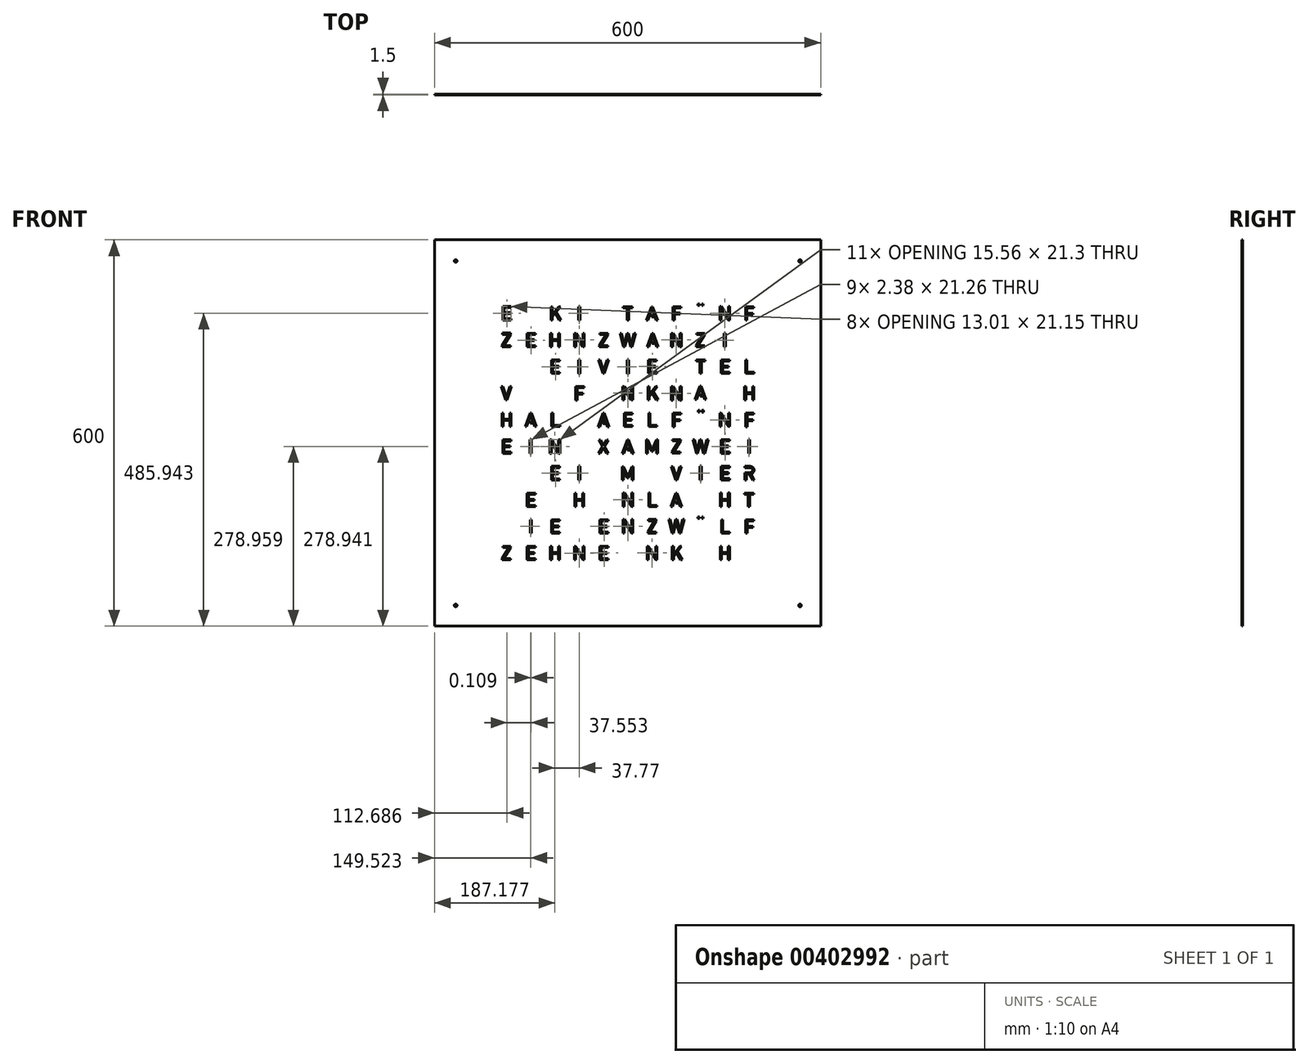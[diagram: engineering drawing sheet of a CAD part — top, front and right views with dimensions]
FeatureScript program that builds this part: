
annotation { "Feature Type Name" : "Feature", "Feature Type Description" : "" }
export const myFeature = defineFeature(function(context is Context, id is Id, definition is map)
    precondition{}
    {
        {
            var Q0;
            Q0=qCreatedBy(makeId("Front.planeOp"),FACE);
            var sketch = newSketch(context, id + "F0", { "sketchPlane" : qUnion([Q0])});
            skLineSegment(sketch, "E0", {"start": v(188.56, 142.8) * mm, "end": v(188.56, 145) * mm});
            skLineSegment(sketch, "E1", {"start": v(188.56, 145) * mm, "end": v(196.13, 145) * mm});
            skLineSegment(sketch, "E2", {"start": v(196.13, 145) * mm, "end": v(196.13, 140.53) * mm});
            skLineSegment(sketch, "E3", {"start": v(188.56, 142.8) * mm, "end": v(194.09, 142.8) * mm});
            skLineSegment(sketch, "E4", {"start": v(194.09, 142.8) * mm, "end": v(194.09, 140.53) * mm});
            skArc(sketch, "E5", {"start": v(183.68, 140.53) * mm, "mid": v(188.88, 135.76) * mm, "end": v(194.09, 140.53) * mm});
            skArc(sketch, "E6", {"start": v(181.41, 140.53) * mm, "mid": v(188.77, 133.64) * mm, "end": v(196.13, 140.53) * mm});
            skLineSegment(sketch, "E7", {"start": v(181.41, 140.53) * mm, "end": v(181.41, 148.36) * mm});
            skLineSegment(sketch, "E8", {"start": v(196.13, 148.36) * mm, "end": v(194.09, 148.36) * mm});
            skLineSegment(sketch, "E9", {"start": v(183.68, 140.53) * mm, "end": v(183.68, 148.36) * mm});
            skArc(sketch, "E10", {"start": v(196.13, 148.36) * mm, "mid": v(188.77, 155.1) * mm, "end": v(181.41, 148.36) * mm});
            skArc(sketch, "E11", {"start": v(194.08, 148.36) * mm, "mid": v(188.88, 153.17) * mm, "end": v(183.68, 148.36) * mm});
            skLineSegment(sketch, "E12", {"start": v(-300, -300) * mm, "end": v(-300, 300) * mm});
            skLineSegment(sketch, "E13", {"start": v(-300, 300) * mm, "end": v(300, 300) * mm});
            skLineSegment(sketch, "E14", {"start": v(300, 300) * mm, "end": v(300, -300) * mm});
            skLineSegment(sketch, "E15", {"start": v(300, -300) * mm, "end": v(-300, -300) * mm});
            skLineSegment(sketch, "E16", {"start": v(149.86, 133.65) * mm, "end": v(149.86, 154.9) * mm});
            skLineSegment(sketch, "E17", {"start": v(149.86, 154.9) * mm, "end": v(152.25, 154.9) * mm});
            skLineSegment(sketch, "E18", {"start": v(152.25, 154.9) * mm, "end": v(152.25, 133.65) * mm});
            skLineSegment(sketch, "E19", {"start": v(152.25, 133.65) * mm, "end": v(149.86, 133.65) * mm});
            skLineSegment(sketch, "E20", {"start": v(107.48, 155) * mm, "end": v(120.12, 155) * mm});
            skLineSegment(sketch, "E21", {"start": v(120.12, 155) * mm, "end": v(120.12, 152.77) * mm});
            skLineSegment(sketch, "E22", {"start": v(120.12, 152.77) * mm, "end": v(109.33, 135.7) * mm});
            skLineSegment(sketch, "E23", {"start": v(109.33, 135.7) * mm, "end": v(119.96, 135.7) * mm});
            skLineSegment(sketch, "E24", {"start": v(119.96, 135.7) * mm, "end": v(119.96, 133.7) * mm});
            skLineSegment(sketch, "E25", {"start": v(119.96, 133.7) * mm, "end": v(106.84, 133.7) * mm});
            skLineSegment(sketch, "E26", {"start": v(106.84, 133.7) * mm, "end": v(106.84, 135.7) * mm});
            skLineSegment(sketch, "E27", {"start": v(106.84, 135.7) * mm, "end": v(117.5, 152.77) * mm});
            skLineSegment(sketch, "E28", {"start": v(117.5, 152.77) * mm, "end": v(107.48, 152.77) * mm});
            skLineSegment(sketch, "E29", {"start": v(107.48, 152.77) * mm, "end": v(107.48, 155) * mm});
            skLineSegment(sketch, "E30", {"start": v(83.43, 133.7) * mm, "end": v(83.43, 155) * mm});
            skLineSegment(sketch, "E31", {"start": v(83.43, 155) * mm, "end": v(81.25, 155) * mm});
            skLineSegment(sketch, "E32", {"start": v(81.25, 155) * mm, "end": v(81.25, 137.64) * mm});
            skLineSegment(sketch, "E33", {"start": v(81.25, 137.64) * mm, "end": v(70.14, 155) * mm});
            skLineSegment(sketch, "E34", {"start": v(70.14, 155) * mm, "end": v(67.87, 155) * mm});
            skLineSegment(sketch, "E35", {"start": v(67.87, 155) * mm, "end": v(67.87, 133.7) * mm});
            skLineSegment(sketch, "E36", {"start": v(67.87, 133.7) * mm, "end": v(70.14, 133.7) * mm});
            skLineSegment(sketch, "E37", {"start": v(70.14, 133.7) * mm, "end": v(70.14, 150.6) * mm});
            skLineSegment(sketch, "E38", {"start": v(70.14, 150.6) * mm, "end": v(81.25, 133.7) * mm});
            skLineSegment(sketch, "E39", {"start": v(81.25, 133.7) * mm, "end": v(83.43, 133.7) * mm});
            skLineSegment(sketch, "E40", {"start": v(38.16, 138.74) * mm, "end": v(38.16, 140.9) * mm});
            skLineSegment(sketch, "E41", {"start": v(38.16, 140.9) * mm, "end": v(42.67, 140.9) * mm});
            skLineSegment(sketch, "E42", {"start": v(38.16, 138.74) * mm, "end": v(43.46, 138.75) * mm});
            skLineSegment(sketch, "E43", {"start": v(47.66, 133.7) * mm, "end": v(45.24, 133.7) * mm});
            skLineSegment(sketch, "E44", {"start": v(45.24, 133.7) * mm, "end": v(43.46, 138.75) * mm});
            skLineSegment(sketch, "E45", {"start": v(39.07, 151.34) * mm, "end": v(32.75, 133.7) * mm});
            skLineSegment(sketch, "E46", {"start": v(32.75, 133.7) * mm, "end": v(30.26, 133.7) * mm});
            skLineSegment(sketch, "E47", {"start": v(30.26, 133.7) * mm, "end": v(38.13, 154.86) * mm});
            skLineSegment(sketch, "E48", {"start": v(38.13, 154.86) * mm, "end": v(39.83, 154.86) * mm});
            skLineSegment(sketch, "E49", {"start": v(39.83, 154.86) * mm, "end": v(47.66, 133.7) * mm});
            skLineSegment(sketch, "E50", {"start": v(42.67, 140.9) * mm, "end": v(39.07, 151.34) * mm});
            skLineSegment(sketch, "E51", {"start": v(6.99, 133.7) * mm, "end": v(4.75, 133.7) * mm});
            skLineSegment(sketch, "E52", {"start": v(4.75, 133.7) * mm, "end": v(0.21, 150.41) * mm});
            skLineSegment(sketch, "E53", {"start": v(0.21, 150.41) * mm, "end": v(-4.4, 133.7) * mm});
            skLineSegment(sketch, "E54", {"start": v(-4.4, 133.7) * mm, "end": v(-6.22, 133.7) * mm});
            skLineSegment(sketch, "E55", {"start": v(-6.22, 133.7) * mm, "end": v(-11.55, 154.84) * mm});
            skLineSegment(sketch, "E56", {"start": v(-11.55, 154.84) * mm, "end": v(-9.36, 154.84) * mm});
            skLineSegment(sketch, "E57", {"start": v(-9.36, 154.84) * mm, "end": v(-5.35, 137.97) * mm});
            skLineSegment(sketch, "E58", {"start": v(-5.35, 137.97) * mm, "end": v(-0.84, 154.84) * mm});
            skLineSegment(sketch, "E59", {"start": v(-0.84, 154.84) * mm, "end": v(1.31, 154.84) * mm});
            skLineSegment(sketch, "E60", {"start": v(1.31, 154.84) * mm, "end": v(5.78, 137.97) * mm});
            skLineSegment(sketch, "E61", {"start": v(5.78, 137.97) * mm, "end": v(10.05, 154.84) * mm});
            skLineSegment(sketch, "E62", {"start": v(10.05, 154.84) * mm, "end": v(12.36, 154.84) * mm});
            skLineSegment(sketch, "E63", {"start": v(12.36, 154.84) * mm, "end": v(6.99, 133.7) * mm});
            skLineSegment(sketch, "E64", {"start": v(-119.95, 133.65) * mm, "end": v(-119.95, 154.8) * mm});
            skLineSegment(sketch, "E65", {"start": v(-119.95, 154.8) * mm, "end": v(-117.8, 154.8) * mm});
            skLineSegment(sketch, "E66", {"start": v(-117.8, 154.8) * mm, "end": v(-117.8, 145.23) * mm});
            skLineSegment(sketch, "E67", {"start": v(-117.8, 145.23) * mm, "end": v(-107.7, 145.23) * mm});
            skLineSegment(sketch, "E68", {"start": v(-107.7, 145.23) * mm, "end": v(-107.7, 154.8) * mm});
            skLineSegment(sketch, "E69", {"start": v(-107.7, 154.8) * mm, "end": v(-105.57, 154.8) * mm});
            skLineSegment(sketch, "E70", {"start": v(-105.57, 154.8) * mm, "end": v(-105.57, 133.65) * mm});
            skLineSegment(sketch, "E71", {"start": v(-105.57, 133.65) * mm, "end": v(-107.7, 133.65) * mm});
            skLineSegment(sketch, "E72", {"start": v(-107.7, 133.65) * mm, "end": v(-107.7, 143.34) * mm});
            skLineSegment(sketch, "E73", {"start": v(-107.7, 143.34) * mm, "end": v(-117.8, 143.34) * mm});
            skLineSegment(sketch, "E74", {"start": v(-117.8, 143.34) * mm, "end": v(-117.8, 133.65) * mm});
            skLineSegment(sketch, "E75", {"start": v(-117.8, 133.65) * mm, "end": v(-119.95, 133.65) * mm});
            skLineSegment(sketch, "E76", {"start": v(-143.25, 133.65) * mm, "end": v(-156.27, 133.65) * mm});
            skLineSegment(sketch, "E77", {"start": v(-156.27, 133.65) * mm, "end": v(-156.27, 154.8) * mm});
            skLineSegment(sketch, "E78", {"start": v(-156.27, 154.8) * mm, "end": v(-143.33, 154.8) * mm});
            skLineSegment(sketch, "E79", {"start": v(-143.33, 154.8) * mm, "end": v(-143.33, 152.78) * mm});
            skLineSegment(sketch, "E80", {"start": v(-143.33, 152.78) * mm, "end": v(-154.07, 152.78) * mm});
            skLineSegment(sketch, "E81", {"start": v(-154.07, 152.78) * mm, "end": v(-154.07, 145.25) * mm});
            skLineSegment(sketch, "E82", {"start": v(-154.07, 145.25) * mm, "end": v(-144.92, 145.25) * mm});
            skLineSegment(sketch, "E83", {"start": v(-144.92, 145.25) * mm, "end": v(-144.92, 143.28) * mm});
            skLineSegment(sketch, "E84", {"start": v(-144.92, 143.28) * mm, "end": v(-154.07, 143.28) * mm});
            skLineSegment(sketch, "E85", {"start": v(-154.07, 143.28) * mm, "end": v(-154.07, 135.67) * mm});
            skLineSegment(sketch, "E86", {"start": v(-154.07, 135.67) * mm, "end": v(-143.25, 135.67) * mm});
            skLineSegment(sketch, "E87", {"start": v(-143.25, 135.67) * mm, "end": v(-143.25, 133.65) * mm});
            skLineSegment(sketch, "E88", {"start": v(-119.17, 175.05) * mm, "end": v(-119.17, 196.27) * mm});
            skLineSegment(sketch, "E89", {"start": v(-119.17, 196.27) * mm, "end": v(-116.98, 196.27) * mm});
            skLineSegment(sketch, "E90", {"start": v(-116.98, 196.27) * mm, "end": v(-116.98, 183.75) * mm});
            skLineSegment(sketch, "E91", {"start": v(-116.98, 183.75) * mm, "end": v(-106.88, 196.27) * mm});
            skLineSegment(sketch, "E92", {"start": v(-106.88, 196.27) * mm, "end": v(-104.38, 196.27) * mm});
            skLineSegment(sketch, "E93", {"start": v(-104.38, 196.27) * mm, "end": v(-111.04, 188.07) * mm});
            skLineSegment(sketch, "E94", {"start": v(-111.04, 188.07) * mm, "end": v(-103.4, 175.05) * mm});
            skLineSegment(sketch, "E95", {"start": v(-103.4, 175.05) * mm, "end": v(-105.9, 175.05) * mm});
            skLineSegment(sketch, "E96", {"start": v(-105.9, 175.05) * mm, "end": v(-112.44, 186.29) * mm});
            skLineSegment(sketch, "E97", {"start": v(-112.44, 186.29) * mm, "end": v(-116.98, 180.61) * mm});
            skLineSegment(sketch, "E98", {"start": v(-116.98, 180.61) * mm, "end": v(-116.98, 175.05) * mm});
            skLineSegment(sketch, "E99", {"start": v(-116.98, 175.05) * mm, "end": v(-119.17, 175.05) * mm});
            skLineSegment(sketch, "E100", {"start": v(-0.86, 175.05) * mm, "end": v(1.57, 175.05) * mm});
            skLineSegment(sketch, "E101", {"start": v(1.57, 175.05) * mm, "end": v(1.57, 194.25) * mm});
            skLineSegment(sketch, "E102", {"start": v(1.57, 194.25) * mm, "end": v(7.58, 194.25) * mm});
            skLineSegment(sketch, "E103", {"start": v(7.58, 194.25) * mm, "end": v(7.58, 196.28) * mm});
            skLineSegment(sketch, "E104", {"start": v(7.58, 196.28) * mm, "end": v(-6.84, 196.28) * mm});
            skLineSegment(sketch, "E105", {"start": v(-6.84, 196.28) * mm, "end": v(-6.84, 194.25) * mm});
            skLineSegment(sketch, "E106", {"start": v(-6.84, 194.25) * mm, "end": v(-0.86, 194.25) * mm});
            skLineSegment(sketch, "E107", {"start": v(-0.86, 194.25) * mm, "end": v(-0.86, 175.05) * mm});
            skLineSegment(sketch, "E108", {"start": v(-67.18, 133.7) * mm, "end": v(-67.18, 155) * mm});
            skLineSegment(sketch, "E109", {"start": v(-67.18, 155) * mm, "end": v(-69.36, 155) * mm});
            skLineSegment(sketch, "E110", {"start": v(-69.36, 155) * mm, "end": v(-69.36, 137.64) * mm});
            skLineSegment(sketch, "E111", {"start": v(-69.36, 137.64) * mm, "end": v(-80.47, 155) * mm});
            skLineSegment(sketch, "E112", {"start": v(-80.47, 155) * mm, "end": v(-82.74, 155) * mm});
            skLineSegment(sketch, "E113", {"start": v(-82.74, 155) * mm, "end": v(-82.74, 133.7) * mm});
            skLineSegment(sketch, "E114", {"start": v(-82.74, 133.7) * mm, "end": v(-80.47, 133.7) * mm});
            skLineSegment(sketch, "E115", {"start": v(-80.47, 133.7) * mm, "end": v(-80.47, 150.6) * mm});
            skLineSegment(sketch, "E116", {"start": v(-80.47, 150.6) * mm, "end": v(-69.36, 133.7) * mm});
            skLineSegment(sketch, "E117", {"start": v(-69.36, 133.7) * mm, "end": v(-67.18, 133.7) * mm});
            skLineSegment(sketch, "E118", {"start": v(-43.37, 155) * mm, "end": v(-30.74, 155) * mm});
            skLineSegment(sketch, "E119", {"start": v(-30.74, 155) * mm, "end": v(-30.74, 152.77) * mm});
            skLineSegment(sketch, "E120", {"start": v(-30.74, 152.77) * mm, "end": v(-41.52, 135.7) * mm});
            skLineSegment(sketch, "E121", {"start": v(-41.52, 135.7) * mm, "end": v(-30.89, 135.7) * mm});
            skLineSegment(sketch, "E122", {"start": v(-30.89, 135.7) * mm, "end": v(-30.89, 133.7) * mm});
            skLineSegment(sketch, "E123", {"start": v(-30.89, 133.7) * mm, "end": v(-44.01, 133.7) * mm});
            skLineSegment(sketch, "E124", {"start": v(-44.01, 133.7) * mm, "end": v(-44.01, 135.7) * mm});
            skLineSegment(sketch, "E125", {"start": v(-44.01, 135.7) * mm, "end": v(-33.35, 152.77) * mm});
            skLineSegment(sketch, "E126", {"start": v(-33.35, 152.77) * mm, "end": v(-43.37, 152.77) * mm});
            skLineSegment(sketch, "E127", {"start": v(-43.37, 152.77) * mm, "end": v(-43.37, 155) * mm});
            skLineSegment(sketch, "E128", {"start": v(-70.28, -14.49) * mm, "end": v(-68.78, -12.92) * mm});
            skLineSegment(sketch, "E129", {"start": v(-82.63, -29.02) * mm, "end": v(-80.97, -27.45) * mm});
            skArc(sketch, "E130", {"start": v(-70.29, -14.49) * mm, "mid": v(-72.17, -13.04) * mm, "end": v(-74.5, -12.5) * mm});
            skArc(sketch, "E131", {"start": v(-68.78, -12.92) * mm, "mid": v(-71.36, -11) * mm, "end": v(-74.5, -10.31) * mm});
            skLineSegment(sketch, "E132", {"start": v(-74.5, -12.5) * mm, "end": v(-76.2, -12.5) * mm});
            skArc(sketch, "E133", {"start": v(-76.2, -12.5) * mm, "mid": v(-79.8, -15.86) * mm, "end": v(-76.68, -19.67) * mm});
            skLineSegment(sketch, "E134", {"start": v(-76.68, -19.67) * mm, "end": v(-72.97, -20.28) * mm});
            skLineSegment(sketch, "E135", {"start": v(-74.5, -10.31) * mm, "end": v(-76.49, -10.31) * mm});
            skArc(sketch, "E136", {"start": v(-76.49, -10.31) * mm, "mid": v(-81.97, -15.85) * mm, "end": v(-76.98, -21.83) * mm});
            skLineSegment(sketch, "E137", {"start": v(-76.98, -21.83) * mm, "end": v(-73.61, -22.28) * mm});
            skArc(sketch, "E138", {"start": v(-80.97, -27.45) * mm, "mid": v(-79.05, -28.97) * mm, "end": v(-76.72, -29.74) * mm});
            skLineSegment(sketch, "E139", {"start": v(-76.72, -29.74) * mm, "end": v(-73.89, -29.74) * mm});
            skArc(sketch, "E140", {"start": v(-73.9, -29.73) * mm, "mid": v(-70.2, -26.14) * mm, "end": v(-73.61, -22.28) * mm});
            skArc(sketch, "E141", {"start": v(-82.63, -29.02) * mm, "mid": v(-79.89, -31.2) * mm, "end": v(-76.48, -31.97) * mm});
            skLineSegment(sketch, "E142", {"start": v(-76.48, -31.97) * mm, "end": v(-73.95, -31.97) * mm});
            skArc(sketch, "E143", {"start": v(-73.95, -31.97) * mm, "mid": v(-68.13, -26.57) * mm, "end": v(-72.97, -20.28) * mm});
            skLineSegment(sketch, "E144", {"start": v(70.3, 196.29) * mm, "end": v(70.3, 174.95) * mm});
            skLineSegment(sketch, "E145", {"start": v(70.3, 174.95) * mm, "end": v(72.58, 174.95) * mm});
            skLineSegment(sketch, "E146", {"start": v(72.58, 174.95) * mm, "end": v(72.58, 184.33) * mm});
            skLineSegment(sketch, "E147", {"start": v(72.58, 184.33) * mm, "end": v(81.7, 184.33) * mm});
            skLineSegment(sketch, "E148", {"start": v(81.7, 184.33) * mm, "end": v(81.7, 186.22) * mm});
            skLineSegment(sketch, "E149", {"start": v(81.7, 186.22) * mm, "end": v(72.58, 186.22) * mm});
            skLineSegment(sketch, "E150", {"start": v(72.58, 186.22) * mm, "end": v(72.58, 194.17) * mm});
            skLineSegment(sketch, "E151", {"start": v(72.58, 194.17) * mm, "end": v(83.24, 194.17) * mm});
            skLineSegment(sketch, "E152", {"start": v(83.24, 194.17) * mm, "end": v(83.24, 196.29) * mm});
            skLineSegment(sketch, "E153", {"start": v(83.24, 196.29) * mm, "end": v(70.3, 196.29) * mm});
            skLineSegment(sketch, "E154", {"start": v(112.3, 92.35) * mm, "end": v(114.73, 92.35) * mm});
            skLineSegment(sketch, "E155", {"start": v(114.73, 92.35) * mm, "end": v(114.73, 111.55) * mm});
            skLineSegment(sketch, "E156", {"start": v(114.73, 111.55) * mm, "end": v(120.74, 111.55) * mm});
            skLineSegment(sketch, "E157", {"start": v(120.74, 111.55) * mm, "end": v(120.74, 113.58) * mm});
            skLineSegment(sketch, "E158", {"start": v(120.74, 113.58) * mm, "end": v(106.32, 113.58) * mm});
            skLineSegment(sketch, "E159", {"start": v(106.32, 113.58) * mm, "end": v(106.32, 111.55) * mm});
            skLineSegment(sketch, "E160", {"start": v(106.32, 111.55) * mm, "end": v(112.3, 111.55) * mm});
            skLineSegment(sketch, "E161", {"start": v(112.3, 111.55) * mm, "end": v(112.3, 92.35) * mm});
            skLineSegment(sketch, "E162", {"start": v(109.41, 200.52) * mm, "end": v(109.41, 197.83) * mm});
            skLineSegment(sketch, "E163", {"start": v(109.41, 197.83) * mm, "end": v(111.54, 197.83) * mm});
            skLineSegment(sketch, "E164", {"start": v(111.54, 197.83) * mm, "end": v(111.54, 200.52) * mm});
            skLineSegment(sketch, "E165", {"start": v(111.54, 200.52) * mm, "end": v(109.41, 200.52) * mm});
            skLineSegment(sketch, "E166", {"start": v(115.37, 200.52) * mm, "end": v(115.37, 197.83) * mm});
            skLineSegment(sketch, "E167", {"start": v(115.37, 197.83) * mm, "end": v(117.5, 197.83) * mm});
            skLineSegment(sketch, "E168", {"start": v(117.5, 197.83) * mm, "end": v(117.5, 200.52) * mm});
            skLineSegment(sketch, "E169", {"start": v(117.5, 200.52) * mm, "end": v(115.37, 200.52) * mm});
            skLineSegment(sketch, "E170", {"start": v(106.2, 181.56) * mm, "end": v(106.2, 196.32) * mm});
            skLineSegment(sketch, "E171", {"start": v(106.2, 196.32) * mm, "end": v(108.28, 196.32) * mm});
            skLineSegment(sketch, "E172", {"start": v(108.28, 196.32) * mm, "end": v(108.28, 181.56) * mm});
            skArc(sketch, "E173", {"start": v(106.2, 181.56) * mm, "mid": v(113.48, 174.84) * mm, "end": v(120.76, 181.56) * mm});
            skArc(sketch, "E174", {"start": v(108.27, 181.56) * mm, "mid": v(113.38, 176.92) * mm, "end": v(118.49, 181.56) * mm});
            skLineSegment(sketch, "E175", {"start": v(118.49, 181.56) * mm, "end": v(118.49, 196.32) * mm});
            skLineSegment(sketch, "E176", {"start": v(118.49, 196.32) * mm, "end": v(120.76, 196.32) * mm});
            skLineSegment(sketch, "E177", {"start": v(120.76, 196.32) * mm, "end": v(120.76, 181.56) * mm});
            skLineSegment(sketch, "E178", {"start": v(183.41, 92.29) * mm, "end": v(183.41, 113.36) * mm});
            skLineSegment(sketch, "E179", {"start": v(183.41, 113.36) * mm, "end": v(185.53, 113.36) * mm});
            skLineSegment(sketch, "E180", {"start": v(185.53, 113.36) * mm, "end": v(185.53, 94.21) * mm});
            skLineSegment(sketch, "E181", {"start": v(185.53, 94.21) * mm, "end": v(196.43, 94.21) * mm});
            skLineSegment(sketch, "E182", {"start": v(196.43, 94.21) * mm, "end": v(196.43, 92.29) * mm});
            skLineSegment(sketch, "E183", {"start": v(196.43, 92.29) * mm, "end": v(183.41, 92.29) * mm});
            skLineSegment(sketch, "E184", {"start": v(156.21, 65.56) * mm, "end": v(158.39, 65.56) * mm});
            skLineSegment(sketch, "E185", {"start": v(156.36, 57.27) * mm, "end": v(158.3, 57.27) * mm});
            skLineSegment(sketch, "E186", {"start": v(146, 65.78) * mm, "end": v(146, 58.67) * mm});
            skLineSegment(sketch, "E187", {"start": v(143.88, 65.56) * mm, "end": v(143.88, 57.16) * mm});
            skArc(sketch, "E188", {"start": v(156.21, 65.56) * mm, "mid": v(151.2, 70.29) * mm, "end": v(146, 65.78) * mm});
            skArc(sketch, "E189", {"start": v(158.39, 65.56) * mm, "mid": v(151.13, 72.37) * mm, "end": v(143.88, 65.55) * mm});
            skArc(sketch, "E190", {"start": v(146, 58.67) * mm, "mid": v(150.5, 52.93) * mm, "end": v(156.36, 57.27) * mm});
            skArc(sketch, "E191", {"start": v(143.88, 57.16) * mm, "mid": v(151.14, 50.64) * mm, "end": v(158.3, 57.27) * mm});
            skLineSegment(sketch, "E192", {"start": v(-38.4, 92.3) * mm, "end": v(-45.18, 113.29) * mm});
            skLineSegment(sketch, "E193", {"start": v(-45.18, 113.29) * mm, "end": v(-42.72, 113.29) * mm});
            skLineSegment(sketch, "E194", {"start": v(-42.72, 113.29) * mm, "end": v(-37.31, 96.53) * mm});
            skLineSegment(sketch, "E195", {"start": v(-37.31, 96.53) * mm, "end": v(-31.86, 113.29) * mm});
            skLineSegment(sketch, "E196", {"start": v(-31.86, 113.29) * mm, "end": v(-29.52, 113.29) * mm});
            skLineSegment(sketch, "E197", {"start": v(-29.52, 113.29) * mm, "end": v(-36.48, 92.3) * mm});
            skLineSegment(sketch, "E198", {"start": v(-36.48, 92.3) * mm, "end": v(-38.4, 92.3) * mm});
            skLineSegment(sketch, "E199", {"start": v(29.1, -31.6) * mm, "end": v(29.1, -10.57) * mm});
            skLineSegment(sketch, "E200", {"start": v(29.1, -10.57) * mm, "end": v(31.14, -10.57) * mm});
            skLineSegment(sketch, "E201", {"start": v(31.14, -10.57) * mm, "end": v(38.06, -26.2) * mm});
            skLineSegment(sketch, "E202", {"start": v(38.06, -26.2) * mm, "end": v(44.87, -10.57) * mm});
            skLineSegment(sketch, "E203", {"start": v(44.87, -10.57) * mm, "end": v(46.77, -10.57) * mm});
            skLineSegment(sketch, "E204", {"start": v(46.77, -10.57) * mm, "end": v(46.77, -31.6) * mm});
            skLineSegment(sketch, "E205", {"start": v(46.77, -31.6) * mm, "end": v(44.87, -31.6) * mm});
            skLineSegment(sketch, "E206", {"start": v(44.87, -31.6) * mm, "end": v(44.87, -15.64) * mm});
            skLineSegment(sketch, "E207", {"start": v(44.87, -15.64) * mm, "end": v(38.97, -28.73) * mm});
            skLineSegment(sketch, "E208", {"start": v(38.97, -28.73) * mm, "end": v(37.2, -28.73) * mm});
            skLineSegment(sketch, "E209", {"start": v(37.2, -28.73) * mm, "end": v(31.07, -15.15) * mm});
            skLineSegment(sketch, "E210", {"start": v(31.07, -15.15) * mm, "end": v(31.07, -31.6) * mm});
            skLineSegment(sketch, "E211", {"start": v(31.07, -31.6) * mm, "end": v(29.1, -31.6) * mm});
            skLineSegment(sketch, "E212", {"start": v(-45.1, -31.67) * mm, "end": v(-42.56, -31.67) * mm});
            skLineSegment(sketch, "E213", {"start": v(-42.56, -31.67) * mm, "end": v(-37.5, -22.97) * mm});
            skLineSegment(sketch, "E214", {"start": v(-37.5, -22.97) * mm, "end": v(-32.38, -31.67) * mm});
            skLineSegment(sketch, "E215", {"start": v(-32.38, -31.67) * mm, "end": v(-29.85, -31.67) * mm});
            skLineSegment(sketch, "E216", {"start": v(-29.85, -31.67) * mm, "end": v(-36.4, -20.96) * mm});
            skLineSegment(sketch, "E217", {"start": v(-36.4, -20.96) * mm, "end": v(-30.2, -10.64) * mm});
            skLineSegment(sketch, "E218", {"start": v(-30.2, -10.64) * mm, "end": v(-32.65, -10.64) * mm});
            skLineSegment(sketch, "E219", {"start": v(-32.65, -10.64) * mm, "end": v(-37.5, -19.11) * mm});
            skLineSegment(sketch, "E220", {"start": v(-37.5, -19.11) * mm, "end": v(-42.22, -10.64) * mm});
            skLineSegment(sketch, "E221", {"start": v(-42.22, -10.64) * mm, "end": v(-44.64, -10.64) * mm});
            skLineSegment(sketch, "E222", {"start": v(-44.64, -10.64) * mm, "end": v(-38.63, -21.08) * mm});
            skLineSegment(sketch, "E223", {"start": v(-38.63, -21.08) * mm, "end": v(-45.1, -31.67) * mm});
            skLineSegment(sketch, "E224", {"start": v(-195.05, 99.84) * mm, "end": v(-195.05, 113.34) * mm});
            skLineSegment(sketch, "E225", {"start": v(-195.05, 113.34) * mm, "end": v(-187, 113.34) * mm});
            skLineSegment(sketch, "E226", {"start": v(-195.05, 99.84) * mm, "end": v(-192.82, 99.84) * mm});
            skLineSegment(sketch, "E227", {"start": v(-192.82, 99.84) * mm, "end": v(-192.82, 111.53) * mm});
            skLineSegment(sketch, "E228", {"start": v(-192.82, 111.53) * mm, "end": v(-187.13, 111.53) * mm});
            skArc(sketch, "E229", {"start": v(-180.57, 106.68) * mm, "mid": v(-182.44, 111.3) * mm, "end": v(-187, 113.34) * mm});
            skArc(sketch, "E230", {"start": v(-182.6, 107.52) * mm, "mid": v(-184.16, 110.32) * mm, "end": v(-187.13, 111.53) * mm});
            skLineSegment(sketch, "E231", {"start": v(-182.6, 107.52) * mm, "end": v(-182.6, 98.82) * mm});
            skLineSegment(sketch, "E232", {"start": v(-180.56, 106.69) * mm, "end": v(-180.56, 98.85) * mm});
            skLineSegment(sketch, "E233", {"start": v(-195.05, 94.35) * mm, "end": v(-195.05, 92.3) * mm});
            skLineSegment(sketch, "E234", {"start": v(-195.05, 92.3) * mm, "end": v(-187.8, 92.3) * mm});
            skLineSegment(sketch, "E235", {"start": v(-195.05, 94.35) * mm, "end": v(-187.24, 94.35) * mm});
            skArc(sketch, "E236", {"start": v(-187.24, 94.35) * mm, "mid": v(-184.08, 95.71) * mm, "end": v(-182.6, 98.82) * mm});
            skArc(sketch, "E237", {"start": v(-187.8, 92.3) * mm, "mid": v(-182.76, 94.01) * mm, "end": v(-180.56, 98.85) * mm});
            skLineSegment(sketch, "E238", {"start": v(-157.03, 92.22) * mm, "end": v(-157.03, 103.9) * mm});
            skLineSegment(sketch, "E239", {"start": v(-157.03, 103.9) * mm, "end": v(-148.43, 103.9) * mm});
            skLineSegment(sketch, "E240", {"start": v(-157.03, 92.22) * mm, "end": v(-154.81, 92.22) * mm});
            skLineSegment(sketch, "E241", {"start": v(-154.81, 92.22) * mm, "end": v(-154.81, 101.87) * mm});
            skLineSegment(sketch, "E242", {"start": v(-154.81, 101.87) * mm, "end": v(-149.84, 101.87) * mm});
            skLineSegment(sketch, "E243", {"start": v(-149.84, 101.87) * mm, "end": v(-144.6, 92.22) * mm});
            skLineSegment(sketch, "E244", {"start": v(-144.6, 92.22) * mm, "end": v(-142.23, 92.22) * mm});
            skLineSegment(sketch, "E245", {"start": v(-142.23, 92.22) * mm, "end": v(-147.3, 101.87) * mm});
            skLineSegment(sketch, "E246", {"start": v(-157.03, 111.42) * mm, "end": v(-157.03, 113.5) * mm});
            skLineSegment(sketch, "E247", {"start": v(-157.03, 113.5) * mm, "end": v(-148.43, 113.5) * mm});
            skLineSegment(sketch, "E248", {"start": v(-157.03, 111.42) * mm, "end": v(-148.43, 111.42) * mm});
            skArc(sketch, "E249", {"start": v(-148.43, 103.9) * mm, "mid": v(-144.78, 107.66) * mm, "end": v(-148.43, 111.42) * mm});
            skArc(sketch, "E250", {"start": v(-147.3, 101.87) * mm, "mid": v(-142.59, 108.2) * mm, "end": v(-148.43, 113.5) * mm});
            skLineSegment(sketch, "E251", {"start": v(-155.58, 64.68) * mm, "end": v(-155.58, 57.75) * mm});
            skLineSegment(sketch, "E252", {"start": v(-157.7, 64.68) * mm, "end": v(-157.7, 57.75) * mm});
            skLineSegment(sketch, "E253", {"start": v(-145.37, 65.17) * mm, "end": v(-145.37, 57.75) * mm});
            skLineSegment(sketch, "E254", {"start": v(-143.2, 65.17) * mm, "end": v(-143.21, 57.75) * mm});
            skArc(sketch, "E255", {"start": v(-155.58, 57.75) * mm, "mid": v(-155.41, 56.44) * mm, "end": v(-154.9, 55.21) * mm});
            skArc(sketch, "E256", {"start": v(-157.7, 57.75) * mm, "mid": v(-157.3, 55.38) * mm, "end": v(-156.15, 53.27) * mm});
            skArc(sketch, "E257", {"start": v(-153.7, 54.12) * mm, "mid": v(-148.36, 53.26) * mm, "end": v(-145.37, 57.75) * mm});
            skArc(sketch, "E258", {"start": v(-154.83, 52.3) * mm, "mid": v(-147.29, 51.33) * mm, "end": v(-143.21, 57.75) * mm});
            skLineSegment(sketch, "E259", {"start": v(-156.14, 53.27) * mm, "end": v(-154.9, 55.21) * mm});
            skLineSegment(sketch, "E260", {"start": v(-154.83, 52.3) * mm, "end": v(-153.7, 54.12) * mm});
            skArc(sketch, "E261", {"start": v(-145.37, 65.17) * mm, "mid": v(-145.6, 66.6) * mm, "end": v(-146.29, 67.9) * mm});
            skArc(sketch, "E262", {"start": v(-143.2, 65.17) * mm, "mid": v(-143.68, 67.56) * mm, "end": v(-144.84, 69.7) * mm});
            skArc(sketch, "E263", {"start": v(-147.3, 69.1) * mm, "mid": v(-152.91, 69.64) * mm, "end": v(-155.58, 64.68) * mm});
            skArc(sketch, "E264", {"start": v(-145.97, 70.65) * mm, "mid": v(-153.74, 71.4) * mm, "end": v(-157.7, 64.68) * mm});
            skLineSegment(sketch, "E265", {"start": v(-147.3, 69.1) * mm, "end": v(-145.97, 70.65) * mm});
            skLineSegment(sketch, "E266", {"start": v(-146.29, 67.9) * mm, "end": v(-144.84, 69.7) * mm});
            skLineSegment(sketch, "E267", {"start": v(-44.45, -73.07) * mm, "end": v(-44.45, -62.49) * mm});
            skLineSegment(sketch, "E268", {"start": v(-44.45, -62.49) * mm, "end": v(-36.7, -62.49) * mm});
            skLineSegment(sketch, "E269", {"start": v(-44.45, -73.07) * mm, "end": v(-42.23, -73.07) * mm});
            skLineSegment(sketch, "E270", {"start": v(-42.23, -73.07) * mm, "end": v(-42.23, -64.5) * mm});
            skLineSegment(sketch, "E271", {"start": v(-42.23, -64.5) * mm, "end": v(-37.26, -64.5) * mm});
            skLineSegment(sketch, "E272", {"start": v(-44.45, -54.16) * mm, "end": v(-44.45, -52.08) * mm});
            skLineSegment(sketch, "E273", {"start": v(-44.45, -52.08) * mm, "end": v(-35.84, -52.08) * mm});
            skLineSegment(sketch, "E274", {"start": v(-44.45, -54.16) * mm, "end": v(-36.41, -54.16) * mm});
            skArc(sketch, "E275", {"start": v(-36.7, -62.49) * mm, "mid": v(-32.22, -58.48) * mm, "end": v(-36.41, -54.16) * mm});
            skArc(sketch, "E276", {"start": v(-37.26, -64.5) * mm, "mid": v(-30.36, -59) * mm, "end": v(-35.84, -52.08) * mm});
            skLineSegment(sketch, "E277", {"start": v(40.45, -67.4) * mm, "end": v(40.45, -52.23) * mm});
            skLineSegment(sketch, "E278", {"start": v(40.45, -52.23) * mm, "end": v(42.6, -52.23) * mm});
            skLineSegment(sketch, "E279", {"start": v(42.6, -52.23) * mm, "end": v(42.6, -66.87) * mm});
            skArc(sketch, "E280", {"start": v(31.45, -71.11) * mm, "mid": v(38.5, -72.85) * mm, "end": v(42.6, -66.87) * mm});
            skArc(sketch, "E281", {"start": v(33, -69.71) * mm, "mid": v(37.48, -71.01) * mm, "end": v(40.45, -67.4) * mm});
            skLineSegment(sketch, "E282", {"start": v(33, -69.71) * mm, "end": v(31.45, -71.11) * mm});
            skLineSegment(sketch, "E283", {"start": v(-81.7, -134.55) * mm, "end": v(-79.86, -134.55) * mm});
            skLineSegment(sketch, "E284", {"start": v(-79.86, -134.55) * mm, "end": v(-79.86, -153.77) * mm});
            skLineSegment(sketch, "E285", {"start": v(-79.86, -153.77) * mm, "end": v(-73.2, -153.77) * mm});
            skLineSegment(sketch, "E286", {"start": v(-81.7, -134.55) * mm, "end": v(-81.7, -155.73) * mm});
            skLineSegment(sketch, "E287", {"start": v(-81.7, -155.73) * mm, "end": v(-73.2, -155.73) * mm});
            skArc(sketch, "E288", {"start": v(-73.2, -153.77) * mm, "mid": v(-69.68, -149.93) * mm, "end": v(-73.2, -146.09) * mm});
            skArc(sketch, "E289", {"start": v(-73.2, -155.73) * mm, "mid": v(-67.5, -151.61) * mm, "end": v(-70.25, -145.14) * mm});
            skArc(sketch, "E290", {"start": v(-70.25, -145.14) * mm, "mid": v(-67.9, -138.67) * mm, "end": v(-73.43, -134.55) * mm});
            skArc(sketch, "E291", {"start": v(-73.2, -144.04) * mm, "mid": v(-69.87, -140.27) * mm, "end": v(-73.43, -136.7) * mm});
            skLineSegment(sketch, "E292", {"start": v(-73.2, -144.04) * mm, "end": v(-77.43, -144.04) * mm});
            skLineSegment(sketch, "E293", {"start": v(-77.43, -144.04) * mm, "end": v(-77.43, -146.09) * mm});
            skLineSegment(sketch, "E294", {"start": v(-77.43, -146.09) * mm, "end": v(-73.2, -146.09) * mm});
            skLineSegment(sketch, "E295", {"start": v(-73.42, -136.7) * mm, "end": v(-77.66, -136.7) * mm});
            skLineSegment(sketch, "E296", {"start": v(-77.66, -136.7) * mm, "end": v(-77.66, -134.55) * mm});
            skLineSegment(sketch, "E297", {"start": v(-77.66, -134.55) * mm, "end": v(-73.42, -134.55) * mm});
            skLineSegment(sketch, "E298", {"start": v(31.5, 51.03) * mm, "end": v(31.5, 72.25) * mm});
            skLineSegment(sketch, "E299", {"start": v(31.5, 72.25) * mm, "end": v(33.69, 72.25) * mm});
            skLineSegment(sketch, "E300", {"start": v(33.69, 72.25) * mm, "end": v(33.69, 59.73) * mm});
            skLineSegment(sketch, "E301", {"start": v(33.69, 59.73) * mm, "end": v(43.8, 72.25) * mm});
            skLineSegment(sketch, "E302", {"start": v(43.8, 72.25) * mm, "end": v(46.29, 72.25) * mm});
            skLineSegment(sketch, "E303", {"start": v(46.29, 72.25) * mm, "end": v(39.63, 64.04) * mm});
            skLineSegment(sketch, "E304", {"start": v(39.63, 64.04) * mm, "end": v(47.27, 51.03) * mm});
            skLineSegment(sketch, "E305", {"start": v(47.27, 51.03) * mm, "end": v(44.78, 51.03) * mm});
            skLineSegment(sketch, "E306", {"start": v(44.78, 51.03) * mm, "end": v(38.23, 62.27) * mm});
            skLineSegment(sketch, "E307", {"start": v(38.23, 62.27) * mm, "end": v(33.69, 56.6) * mm});
            skLineSegment(sketch, "E308", {"start": v(33.69, 56.6) * mm, "end": v(33.69, 51.03) * mm});
            skLineSegment(sketch, "E309", {"start": v(33.69, 51.03) * mm, "end": v(31.5, 51.03) * mm});
            skLineSegment(sketch, "E310", {"start": v(69.12, -197.17) * mm, "end": v(69.12, -175.95) * mm});
            skLineSegment(sketch, "E311", {"start": v(69.12, -175.95) * mm, "end": v(71.32, -175.95) * mm});
            skLineSegment(sketch, "E312", {"start": v(71.32, -175.95) * mm, "end": v(71.32, -188.47) * mm});
            skLineSegment(sketch, "E313", {"start": v(71.32, -188.47) * mm, "end": v(81.42, -175.95) * mm});
            skLineSegment(sketch, "E314", {"start": v(81.42, -175.95) * mm, "end": v(83.92, -175.95) * mm});
            skLineSegment(sketch, "E315", {"start": v(83.92, -175.95) * mm, "end": v(77.26, -184.16) * mm});
            skLineSegment(sketch, "E316", {"start": v(77.26, -184.16) * mm, "end": v(84.9, -197.17) * mm});
            skLineSegment(sketch, "E317", {"start": v(84.9, -197.17) * mm, "end": v(82.4, -197.17) * mm});
            skLineSegment(sketch, "E318", {"start": v(82.4, -197.17) * mm, "end": v(75.86, -185.94) * mm});
            skLineSegment(sketch, "E319", {"start": v(75.86, -185.94) * mm, "end": v(71.32, -191.61) * mm});
            skLineSegment(sketch, "E320", {"start": v(71.32, -191.61) * mm, "end": v(71.32, -197.17) * mm});
            skLineSegment(sketch, "E321", {"start": v(71.32, -197.17) * mm, "end": v(69.12, -197.17) * mm});
            skLineSegment(sketch, "E322", {"start": v(183.2, 196.2) * mm, "end": v(183.2, 174.87) * mm});
            skLineSegment(sketch, "E323", {"start": v(183.2, 174.87) * mm, "end": v(185.48, 174.87) * mm});
            skLineSegment(sketch, "E324", {"start": v(185.48, 174.87) * mm, "end": v(185.48, 184.25) * mm});
            skLineSegment(sketch, "E325", {"start": v(185.48, 184.25) * mm, "end": v(194.6, 184.25) * mm});
            skLineSegment(sketch, "E326", {"start": v(194.6, 184.25) * mm, "end": v(194.6, 186.14) * mm});
            skLineSegment(sketch, "E327", {"start": v(194.6, 186.14) * mm, "end": v(185.48, 186.14) * mm});
            skLineSegment(sketch, "E328", {"start": v(185.48, 186.14) * mm, "end": v(185.48, 194.09) * mm});
            skLineSegment(sketch, "E329", {"start": v(185.48, 194.09) * mm, "end": v(196.15, 194.09) * mm});
            skLineSegment(sketch, "E330", {"start": v(196.15, 194.09) * mm, "end": v(196.15, 196.2) * mm});
            skLineSegment(sketch, "E331", {"start": v(196.15, 196.2) * mm, "end": v(183.2, 196.2) * mm});
            skLineSegment(sketch, "E332", {"start": v(70.3, 30.92) * mm, "end": v(70.3, 9.58) * mm});
            skLineSegment(sketch, "E333", {"start": v(70.3, 9.58) * mm, "end": v(72.57, 9.58) * mm});
            skLineSegment(sketch, "E334", {"start": v(72.57, 9.58) * mm, "end": v(72.57, 18.96) * mm});
            skLineSegment(sketch, "E335", {"start": v(72.57, 18.96) * mm, "end": v(81.69, 18.96) * mm});
            skLineSegment(sketch, "E336", {"start": v(81.69, 18.96) * mm, "end": v(81.69, 20.85) * mm});
            skLineSegment(sketch, "E337", {"start": v(81.69, 20.85) * mm, "end": v(72.57, 20.85) * mm});
            skLineSegment(sketch, "E338", {"start": v(72.57, 20.85) * mm, "end": v(72.57, 28.8) * mm});
            skLineSegment(sketch, "E339", {"start": v(72.57, 28.8) * mm, "end": v(83.24, 28.8) * mm});
            skLineSegment(sketch, "E340", {"start": v(83.24, 28.8) * mm, "end": v(83.24, 30.92) * mm});
            skLineSegment(sketch, "E341", {"start": v(83.24, 30.92) * mm, "end": v(70.3, 30.92) * mm});
            skLineSegment(sketch, "E342", {"start": v(183.42, 30.94) * mm, "end": v(183.42, 9.6) * mm});
            skLineSegment(sketch, "E343", {"start": v(183.42, 9.6) * mm, "end": v(185.7, 9.6) * mm});
            skLineSegment(sketch, "E344", {"start": v(185.7, 9.6) * mm, "end": v(185.7, 18.98) * mm});
            skLineSegment(sketch, "E345", {"start": v(185.7, 18.98) * mm, "end": v(194.81, 18.98) * mm});
            skLineSegment(sketch, "E346", {"start": v(194.81, 18.98) * mm, "end": v(194.81, 20.88) * mm});
            skLineSegment(sketch, "E347", {"start": v(194.81, 20.88) * mm, "end": v(185.7, 20.88) * mm});
            skLineSegment(sketch, "E348", {"start": v(185.7, 20.88) * mm, "end": v(185.7, 28.82) * mm});
            skLineSegment(sketch, "E349", {"start": v(185.7, 28.82) * mm, "end": v(196.36, 28.82) * mm});
            skLineSegment(sketch, "E350", {"start": v(196.36, 28.82) * mm, "end": v(196.36, 30.94) * mm});
            skLineSegment(sketch, "E351", {"start": v(196.36, 30.94) * mm, "end": v(183.42, 30.94) * mm});
            skLineSegment(sketch, "E352", {"start": v(109.56, 35.25) * mm, "end": v(109.56, 32.55) * mm});
            skLineSegment(sketch, "E353", {"start": v(109.56, 32.55) * mm, "end": v(111.7, 32.55) * mm});
            skLineSegment(sketch, "E354", {"start": v(111.7, 32.55) * mm, "end": v(111.7, 35.25) * mm});
            skLineSegment(sketch, "E355", {"start": v(111.7, 35.25) * mm, "end": v(109.56, 35.25) * mm});
            skLineSegment(sketch, "E356", {"start": v(115.52, 35.25) * mm, "end": v(115.52, 32.55) * mm});
            skLineSegment(sketch, "E357", {"start": v(115.52, 32.55) * mm, "end": v(117.65, 32.55) * mm});
            skLineSegment(sketch, "E358", {"start": v(117.65, 32.55) * mm, "end": v(117.65, 35.25) * mm});
            skLineSegment(sketch, "E359", {"start": v(117.65, 35.25) * mm, "end": v(115.52, 35.25) * mm});
            skLineSegment(sketch, "E360", {"start": v(106.35, 16.28) * mm, "end": v(106.35, 31.04) * mm});
            skLineSegment(sketch, "E361", {"start": v(106.35, 31.04) * mm, "end": v(108.43, 31.04) * mm});
            skLineSegment(sketch, "E362", {"start": v(108.43, 31.04) * mm, "end": v(108.43, 16.28) * mm});
            skArc(sketch, "E363", {"start": v(106.35, 16.28) * mm, "mid": v(113.63, 9.57) * mm, "end": v(120.91, 16.28) * mm});
            skArc(sketch, "E364", {"start": v(108.43, 16.28) * mm, "mid": v(113.53, 11.65) * mm, "end": v(118.64, 16.28) * mm});
            skLineSegment(sketch, "E365", {"start": v(118.64, 16.28) * mm, "end": v(118.64, 31.04) * mm});
            skLineSegment(sketch, "E366", {"start": v(118.64, 31.04) * mm, "end": v(120.91, 31.04) * mm});
            skLineSegment(sketch, "E367", {"start": v(120.91, 31.04) * mm, "end": v(120.91, 16.28) * mm});
            skLineSegment(sketch, "E368", {"start": v(-194.18, 155.16) * mm, "end": v(-181.55, 155.16) * mm});
            skLineSegment(sketch, "E369", {"start": v(-181.55, 155.16) * mm, "end": v(-181.55, 152.93) * mm});
            skLineSegment(sketch, "E370", {"start": v(-181.55, 152.93) * mm, "end": v(-192.33, 135.87) * mm});
            skLineSegment(sketch, "E371", {"start": v(-192.33, 135.87) * mm, "end": v(-181.7, 135.87) * mm});
            skLineSegment(sketch, "E372", {"start": v(-181.7, 135.87) * mm, "end": v(-181.7, 133.86) * mm});
            skLineSegment(sketch, "E373", {"start": v(-181.7, 133.86) * mm, "end": v(-194.83, 133.86) * mm});
            skLineSegment(sketch, "E374", {"start": v(-194.83, 133.86) * mm, "end": v(-194.83, 135.87) * mm});
            skLineSegment(sketch, "E375", {"start": v(-194.83, 135.87) * mm, "end": v(-184.16, 152.93) * mm});
            skLineSegment(sketch, "E376", {"start": v(-184.16, 152.93) * mm, "end": v(-194.18, 152.93) * mm});
            skLineSegment(sketch, "E377", {"start": v(-194.18, 152.93) * mm, "end": v(-194.18, 155.16) * mm});
            skLineSegment(sketch, "E378", {"start": v(69.56, -10.27) * mm, "end": v(82.2, -10.27) * mm});
            skLineSegment(sketch, "E379", {"start": v(82.2, -10.27) * mm, "end": v(82.2, -12.5) * mm});
            skLineSegment(sketch, "E380", {"start": v(82.2, -12.5) * mm, "end": v(71.42, -29.57) * mm});
            skLineSegment(sketch, "E381", {"start": v(71.42, -29.57) * mm, "end": v(82.05, -29.57) * mm});
            skLineSegment(sketch, "E382", {"start": v(82.05, -29.57) * mm, "end": v(82.05, -31.57) * mm});
            skLineSegment(sketch, "E383", {"start": v(82.05, -31.57) * mm, "end": v(68.92, -31.57) * mm});
            skLineSegment(sketch, "E384", {"start": v(68.92, -31.57) * mm, "end": v(68.92, -29.57) * mm});
            skLineSegment(sketch, "E385", {"start": v(68.92, -29.57) * mm, "end": v(79.59, -12.5) * mm});
            skLineSegment(sketch, "E386", {"start": v(79.59, -12.5) * mm, "end": v(69.56, -12.5) * mm});
            skLineSegment(sketch, "E387", {"start": v(69.56, -12.5) * mm, "end": v(69.56, -10.27) * mm});
            skLineSegment(sketch, "E388", {"start": v(31.98, -134.37) * mm, "end": v(44.62, -134.37) * mm});
            skLineSegment(sketch, "E389", {"start": v(44.62, -134.37) * mm, "end": v(44.62, -136.6) * mm});
            skLineSegment(sketch, "E390", {"start": v(44.62, -136.6) * mm, "end": v(33.83, -153.66) * mm});
            skLineSegment(sketch, "E391", {"start": v(33.83, -153.66) * mm, "end": v(44.46, -153.66) * mm});
            skLineSegment(sketch, "E392", {"start": v(44.46, -153.66) * mm, "end": v(44.46, -155.67) * mm});
            skLineSegment(sketch, "E393", {"start": v(44.46, -155.67) * mm, "end": v(31.34, -155.67) * mm});
            skLineSegment(sketch, "E394", {"start": v(31.34, -155.67) * mm, "end": v(31.34, -153.66) * mm});
            skLineSegment(sketch, "E395", {"start": v(31.34, -153.66) * mm, "end": v(42, -136.6) * mm});
            skLineSegment(sketch, "E396", {"start": v(42, -136.6) * mm, "end": v(31.98, -136.6) * mm});
            skLineSegment(sketch, "E397", {"start": v(31.98, -136.6) * mm, "end": v(31.98, -134.37) * mm});
            skLineSegment(sketch, "E398", {"start": v(-194.13, -175.8) * mm, "end": v(-181.5, -175.8) * mm});
            skLineSegment(sketch, "E399", {"start": v(-181.5, -175.8) * mm, "end": v(-181.5, -178.03) * mm});
            skLineSegment(sketch, "E400", {"start": v(-181.5, -178.03) * mm, "end": v(-192.28, -195.1) * mm});
            skLineSegment(sketch, "E401", {"start": v(-192.28, -195.1) * mm, "end": v(-181.65, -195.1) * mm});
            skLineSegment(sketch, "E402", {"start": v(-181.65, -195.1) * mm, "end": v(-181.65, -197.1) * mm});
            skLineSegment(sketch, "E403", {"start": v(-181.65, -197.1) * mm, "end": v(-194.77, -197.1) * mm});
            skLineSegment(sketch, "E404", {"start": v(-194.77, -197.1) * mm, "end": v(-194.77, -195.1) * mm});
            skLineSegment(sketch, "E405", {"start": v(-194.77, -195.1) * mm, "end": v(-184.1, -178.03) * mm});
            skLineSegment(sketch, "E406", {"start": v(-184.1, -178.03) * mm, "end": v(-194.13, -178.03) * mm});
            skLineSegment(sketch, "E407", {"start": v(-194.13, -178.03) * mm, "end": v(-194.13, -175.8) * mm});
            skLineSegment(sketch, "E408", {"start": v(-180.8, 175.37) * mm, "end": v(-193.82, 175.37) * mm});
            skLineSegment(sketch, "E409", {"start": v(-193.82, 175.37) * mm, "end": v(-193.82, 196.52) * mm});
            skLineSegment(sketch, "E410", {"start": v(-193.82, 196.52) * mm, "end": v(-180.88, 196.52) * mm});
            skLineSegment(sketch, "E411", {"start": v(-180.88, 196.52) * mm, "end": v(-180.88, 194.5) * mm});
            skLineSegment(sketch, "E412", {"start": v(-180.88, 194.5) * mm, "end": v(-191.63, 194.5) * mm});
            skLineSegment(sketch, "E413", {"start": v(-191.63, 194.5) * mm, "end": v(-191.63, 186.96) * mm});
            skLineSegment(sketch, "E414", {"start": v(-191.63, 186.96) * mm, "end": v(-182.47, 186.96) * mm});
            skLineSegment(sketch, "E415", {"start": v(-182.47, 186.96) * mm, "end": v(-182.47, 185) * mm});
            skLineSegment(sketch, "E416", {"start": v(-182.47, 185) * mm, "end": v(-191.63, 185) * mm});
            skLineSegment(sketch, "E417", {"start": v(-191.63, 185) * mm, "end": v(-191.63, 177.4) * mm});
            skLineSegment(sketch, "E418", {"start": v(-191.63, 177.4) * mm, "end": v(-180.8, 177.4) * mm});
            skLineSegment(sketch, "E419", {"start": v(-180.8, 177.4) * mm, "end": v(-180.8, 175.37) * mm});
            skLineSegment(sketch, "E420", {"start": v(-105.45, 92.43) * mm, "end": v(-118.46, 92.43) * mm});
            skLineSegment(sketch, "E421", {"start": v(-118.46, 92.43) * mm, "end": v(-118.46, 113.58) * mm});
            skLineSegment(sketch, "E422", {"start": v(-118.46, 113.58) * mm, "end": v(-105.53, 113.58) * mm});
            skLineSegment(sketch, "E423", {"start": v(-105.53, 113.58) * mm, "end": v(-105.53, 111.56) * mm});
            skLineSegment(sketch, "E424", {"start": v(-105.53, 111.56) * mm, "end": v(-116.27, 111.56) * mm});
            skLineSegment(sketch, "E425", {"start": v(-116.27, 111.56) * mm, "end": v(-116.27, 104.03) * mm});
            skLineSegment(sketch, "E426", {"start": v(-116.27, 104.03) * mm, "end": v(-107.11, 104.03) * mm});
            skLineSegment(sketch, "E427", {"start": v(-107.11, 104.03) * mm, "end": v(-107.11, 102.06) * mm});
            skLineSegment(sketch, "E428", {"start": v(-107.11, 102.06) * mm, "end": v(-116.27, 102.06) * mm});
            skLineSegment(sketch, "E429", {"start": v(-116.27, 102.06) * mm, "end": v(-116.27, 94.46) * mm});
            skLineSegment(sketch, "E430", {"start": v(-116.27, 94.46) * mm, "end": v(-105.45, 94.46) * mm});
            skLineSegment(sketch, "E431", {"start": v(-105.45, 94.46) * mm, "end": v(-105.45, 92.43) * mm});
            skLineSegment(sketch, "E432", {"start": v(45.33, 92.51) * mm, "end": v(32.32, 92.51) * mm});
            skLineSegment(sketch, "E433", {"start": v(32.32, 92.51) * mm, "end": v(32.32, 113.66) * mm});
            skLineSegment(sketch, "E434", {"start": v(32.32, 113.66) * mm, "end": v(45.25, 113.66) * mm});
            skLineSegment(sketch, "E435", {"start": v(45.25, 113.66) * mm, "end": v(45.25, 111.63) * mm});
            skLineSegment(sketch, "E436", {"start": v(45.25, 111.63) * mm, "end": v(34.5, 111.63) * mm});
            skLineSegment(sketch, "E437", {"start": v(34.5, 111.63) * mm, "end": v(34.5, 104.1) * mm});
            skLineSegment(sketch, "E438", {"start": v(34.5, 104.1) * mm, "end": v(43.67, 104.1) * mm});
            skLineSegment(sketch, "E439", {"start": v(43.67, 104.1) * mm, "end": v(43.67, 102.14) * mm});
            skLineSegment(sketch, "E440", {"start": v(43.67, 102.14) * mm, "end": v(34.5, 102.14) * mm});
            skLineSegment(sketch, "E441", {"start": v(34.5, 102.14) * mm, "end": v(34.5, 94.53) * mm});
            skLineSegment(sketch, "E442", {"start": v(34.5, 94.53) * mm, "end": v(45.33, 94.53) * mm});
            skLineSegment(sketch, "E443", {"start": v(45.33, 94.53) * mm, "end": v(45.33, 92.51) * mm});
            skLineSegment(sketch, "E444", {"start": v(158.47, 92.53) * mm, "end": v(145.46, 92.53) * mm});
            skLineSegment(sketch, "E445", {"start": v(145.46, 92.53) * mm, "end": v(145.46, 113.68) * mm});
            skLineSegment(sketch, "E446", {"start": v(145.46, 113.68) * mm, "end": v(158.4, 113.68) * mm});
            skLineSegment(sketch, "E447", {"start": v(158.4, 113.68) * mm, "end": v(158.4, 111.65) * mm});
            skLineSegment(sketch, "E448", {"start": v(158.4, 111.65) * mm, "end": v(147.65, 111.65) * mm});
            skLineSegment(sketch, "E449", {"start": v(147.65, 111.65) * mm, "end": v(147.65, 104.12) * mm});
            skLineSegment(sketch, "E450", {"start": v(147.65, 104.12) * mm, "end": v(156.8, 104.12) * mm});
            skLineSegment(sketch, "E451", {"start": v(156.8, 104.12) * mm, "end": v(156.8, 102.15) * mm});
            skLineSegment(sketch, "E452", {"start": v(156.8, 102.15) * mm, "end": v(147.65, 102.15) * mm});
            skLineSegment(sketch, "E453", {"start": v(147.65, 102.15) * mm, "end": v(147.65, 94.55) * mm});
            skLineSegment(sketch, "E454", {"start": v(147.65, 94.55) * mm, "end": v(158.47, 94.55) * mm});
            skLineSegment(sketch, "E455", {"start": v(158.47, 94.55) * mm, "end": v(158.47, 92.53) * mm});
            skLineSegment(sketch, "E456", {"start": v(7.62, 9.72) * mm, "end": v(-5.4, 9.72) * mm});
            skLineSegment(sketch, "E457", {"start": v(-5.4, 9.72) * mm, "end": v(-5.4, 30.87) * mm});
            skLineSegment(sketch, "E458", {"start": v(-5.4, 30.87) * mm, "end": v(7.54, 30.87) * mm});
            skLineSegment(sketch, "E459", {"start": v(7.54, 30.87) * mm, "end": v(7.54, 28.85) * mm});
            skLineSegment(sketch, "E460", {"start": v(7.54, 28.85) * mm, "end": v(-3.2, 28.85) * mm});
            skLineSegment(sketch, "E461", {"start": v(-3.2, 28.85) * mm, "end": v(-3.2, 21.32) * mm});
            skLineSegment(sketch, "E462", {"start": v(-3.2, 21.32) * mm, "end": v(5.95, 21.32) * mm});
            skLineSegment(sketch, "E463", {"start": v(5.95, 21.32) * mm, "end": v(5.95, 19.35) * mm});
            skLineSegment(sketch, "E464", {"start": v(5.95, 19.35) * mm, "end": v(-3.2, 19.35) * mm});
            skLineSegment(sketch, "E465", {"start": v(-3.2, 19.35) * mm, "end": v(-3.2, 11.74) * mm});
            skLineSegment(sketch, "E466", {"start": v(-3.2, 11.74) * mm, "end": v(7.62, 11.74) * mm});
            skLineSegment(sketch, "E467", {"start": v(7.62, 11.74) * mm, "end": v(7.62, 9.72) * mm});
            skLineSegment(sketch, "E468", {"start": v(-180.77, -31.66) * mm, "end": v(-193.79, -31.66) * mm});
            skLineSegment(sketch, "E469", {"start": v(-193.79, -31.66) * mm, "end": v(-193.79, -10.5) * mm});
            skLineSegment(sketch, "E470", {"start": v(-193.79, -10.5) * mm, "end": v(-180.85, -10.5) * mm});
            skLineSegment(sketch, "E471", {"start": v(-180.85, -10.5) * mm, "end": v(-180.85, -12.54) * mm});
            skLineSegment(sketch, "E472", {"start": v(-180.85, -12.54) * mm, "end": v(-191.6, -12.54) * mm});
            skLineSegment(sketch, "E473", {"start": v(-191.6, -12.54) * mm, "end": v(-191.6, -20.06) * mm});
            skLineSegment(sketch, "E474", {"start": v(-191.6, -20.06) * mm, "end": v(-182.44, -20.06) * mm});
            skLineSegment(sketch, "E475", {"start": v(-182.44, -20.06) * mm, "end": v(-182.44, -22.03) * mm});
            skLineSegment(sketch, "E476", {"start": v(-182.44, -22.03) * mm, "end": v(-191.6, -22.03) * mm});
            skLineSegment(sketch, "E477", {"start": v(-191.6, -22.03) * mm, "end": v(-191.6, -29.64) * mm});
            skLineSegment(sketch, "E478", {"start": v(-191.6, -29.64) * mm, "end": v(-180.77, -29.64) * mm});
            skLineSegment(sketch, "E479", {"start": v(-180.77, -29.64) * mm, "end": v(-180.77, -31.66) * mm});
            skLineSegment(sketch, "E480", {"start": v(158.38, -31.6) * mm, "end": v(145.37, -31.6) * mm});
            skLineSegment(sketch, "E481", {"start": v(145.37, -31.6) * mm, "end": v(145.37, -10.44) * mm});
            skLineSegment(sketch, "E482", {"start": v(145.37, -10.44) * mm, "end": v(158.3, -10.44) * mm});
            skLineSegment(sketch, "E483", {"start": v(158.3, -10.44) * mm, "end": v(158.3, -12.47) * mm});
            skLineSegment(sketch, "E484", {"start": v(158.3, -12.47) * mm, "end": v(147.56, -12.47) * mm});
            skLineSegment(sketch, "E485", {"start": v(147.56, -12.47) * mm, "end": v(147.56, -20) * mm});
            skLineSegment(sketch, "E486", {"start": v(147.56, -20) * mm, "end": v(156.72, -20) * mm});
            skLineSegment(sketch, "E487", {"start": v(156.72, -20) * mm, "end": v(156.72, -21.97) * mm});
            skLineSegment(sketch, "E488", {"start": v(156.72, -21.97) * mm, "end": v(147.56, -21.97) * mm});
            skLineSegment(sketch, "E489", {"start": v(147.56, -21.97) * mm, "end": v(147.56, -29.57) * mm});
            skLineSegment(sketch, "E490", {"start": v(147.56, -29.57) * mm, "end": v(158.38, -29.57) * mm});
            skLineSegment(sketch, "E491", {"start": v(158.38, -29.57) * mm, "end": v(158.38, -31.6) * mm});
            skLineSegment(sketch, "E492", {"start": v(158.44, -72.96) * mm, "end": v(145.42, -72.96) * mm});
            skLineSegment(sketch, "E493", {"start": v(145.42, -72.96) * mm, "end": v(145.42, -51.81) * mm});
            skLineSegment(sketch, "E494", {"start": v(145.42, -51.81) * mm, "end": v(158.36, -51.81) * mm});
            skLineSegment(sketch, "E495", {"start": v(158.36, -51.81) * mm, "end": v(158.36, -53.84) * mm});
            skLineSegment(sketch, "E496", {"start": v(158.36, -53.84) * mm, "end": v(147.62, -53.84) * mm});
            skLineSegment(sketch, "E497", {"start": v(147.62, -53.84) * mm, "end": v(147.62, -61.37) * mm});
            skLineSegment(sketch, "E498", {"start": v(147.62, -61.37) * mm, "end": v(156.77, -61.37) * mm});
            skLineSegment(sketch, "E499", {"start": v(156.77, -61.37) * mm, "end": v(156.77, -63.34) * mm});
            skLineSegment(sketch, "E500", {"start": v(156.77, -63.34) * mm, "end": v(147.62, -63.34) * mm});
            skLineSegment(sketch, "E501", {"start": v(147.62, -63.34) * mm, "end": v(147.62, -70.94) * mm});
            skLineSegment(sketch, "E502", {"start": v(147.62, -70.94) * mm, "end": v(158.44, -70.94) * mm});
            skLineSegment(sketch, "E503", {"start": v(158.44, -70.94) * mm, "end": v(158.44, -72.96) * mm});
            skLineSegment(sketch, "E504", {"start": v(-143.2, -114.39) * mm, "end": v(-156.22, -114.39) * mm});
            skLineSegment(sketch, "E505", {"start": v(-156.22, -114.39) * mm, "end": v(-156.22, -93.24) * mm});
            skLineSegment(sketch, "E506", {"start": v(-156.22, -93.24) * mm, "end": v(-143.28, -93.24) * mm});
            skLineSegment(sketch, "E507", {"start": v(-143.28, -93.24) * mm, "end": v(-143.28, -95.27) * mm});
            skLineSegment(sketch, "E508", {"start": v(-143.28, -95.27) * mm, "end": v(-154.02, -95.27) * mm});
            skLineSegment(sketch, "E509", {"start": v(-154.02, -95.27) * mm, "end": v(-154.02, -102.8) * mm});
            skLineSegment(sketch, "E510", {"start": v(-154.02, -102.8) * mm, "end": v(-144.86, -102.8) * mm});
            skLineSegment(sketch, "E511", {"start": v(-144.86, -102.8) * mm, "end": v(-144.86, -104.76) * mm});
            skLineSegment(sketch, "E512", {"start": v(-144.86, -104.76) * mm, "end": v(-154.02, -104.76) * mm});
            skLineSegment(sketch, "E513", {"start": v(-154.02, -104.76) * mm, "end": v(-154.02, -112.37) * mm});
            skLineSegment(sketch, "E514", {"start": v(-154.02, -112.37) * mm, "end": v(-143.2, -112.37) * mm});
            skLineSegment(sketch, "E515", {"start": v(-143.2, -112.37) * mm, "end": v(-143.2, -114.39) * mm});
            skLineSegment(sketch, "E516", {"start": v(-105.37, -155.7) * mm, "end": v(-118.38, -155.7) * mm});
            skLineSegment(sketch, "E517", {"start": v(-118.38, -155.7) * mm, "end": v(-118.38, -134.56) * mm});
            skLineSegment(sketch, "E518", {"start": v(-118.38, -134.56) * mm, "end": v(-105.45, -134.56) * mm});
            skLineSegment(sketch, "E519", {"start": v(-105.45, -134.56) * mm, "end": v(-105.45, -136.58) * mm});
            skLineSegment(sketch, "E520", {"start": v(-105.45, -136.58) * mm, "end": v(-116.2, -136.58) * mm});
            skLineSegment(sketch, "E521", {"start": v(-116.2, -136.58) * mm, "end": v(-116.2, -144.11) * mm});
            skLineSegment(sketch, "E522", {"start": v(-116.2, -144.11) * mm, "end": v(-107.03, -144.11) * mm});
            skLineSegment(sketch, "E523", {"start": v(-107.03, -144.11) * mm, "end": v(-107.03, -146.08) * mm});
            skLineSegment(sketch, "E524", {"start": v(-107.03, -146.08) * mm, "end": v(-116.2, -146.08) * mm});
            skLineSegment(sketch, "E525", {"start": v(-116.2, -146.08) * mm, "end": v(-116.2, -153.69) * mm});
            skLineSegment(sketch, "E526", {"start": v(-116.2, -153.69) * mm, "end": v(-105.37, -153.69) * mm});
            skLineSegment(sketch, "E527", {"start": v(-105.37, -153.69) * mm, "end": v(-105.37, -155.7) * mm});
            skLineSegment(sketch, "E528", {"start": v(-30, -155.65) * mm, "end": v(-43.02, -155.65) * mm});
            skLineSegment(sketch, "E529", {"start": v(-43.02, -155.65) * mm, "end": v(-43.02, -134.5) * mm});
            skLineSegment(sketch, "E530", {"start": v(-43.02, -134.5) * mm, "end": v(-30.08, -134.5) * mm});
            skLineSegment(sketch, "E531", {"start": v(-30.08, -134.5) * mm, "end": v(-30.08, -136.53) * mm});
            skLineSegment(sketch, "E532", {"start": v(-30.08, -136.53) * mm, "end": v(-40.83, -136.53) * mm});
            skLineSegment(sketch, "E533", {"start": v(-40.83, -136.53) * mm, "end": v(-40.83, -144.06) * mm});
            skLineSegment(sketch, "E534", {"start": v(-40.83, -144.06) * mm, "end": v(-31.67, -144.06) * mm});
            skLineSegment(sketch, "E535", {"start": v(-31.67, -144.06) * mm, "end": v(-31.67, -146.02) * mm});
            skLineSegment(sketch, "E536", {"start": v(-31.67, -146.02) * mm, "end": v(-40.83, -146.02) * mm});
            skLineSegment(sketch, "E537", {"start": v(-40.83, -146.02) * mm, "end": v(-40.83, -153.63) * mm});
            skLineSegment(sketch, "E538", {"start": v(-40.83, -153.63) * mm, "end": v(-30, -153.63) * mm});
            skLineSegment(sketch, "E539", {"start": v(-30, -153.63) * mm, "end": v(-30, -155.65) * mm});
            skLineSegment(sketch, "E540", {"start": v(-143.03, -197.11) * mm, "end": v(-156.05, -197.11) * mm});
            skLineSegment(sketch, "E541", {"start": v(-156.05, -197.11) * mm, "end": v(-156.05, -175.96) * mm});
            skLineSegment(sketch, "E542", {"start": v(-156.05, -175.96) * mm, "end": v(-143.11, -175.96) * mm});
            skLineSegment(sketch, "E543", {"start": v(-143.11, -175.96) * mm, "end": v(-143.11, -177.99) * mm});
            skLineSegment(sketch, "E544", {"start": v(-143.11, -177.99) * mm, "end": v(-153.85, -177.99) * mm});
            skLineSegment(sketch, "E545", {"start": v(-153.85, -177.99) * mm, "end": v(-153.85, -185.52) * mm});
            skLineSegment(sketch, "E546", {"start": v(-153.85, -185.52) * mm, "end": v(-144.7, -185.52) * mm});
            skLineSegment(sketch, "E547", {"start": v(-144.7, -185.52) * mm, "end": v(-144.7, -187.49) * mm});
            skLineSegment(sketch, "E548", {"start": v(-144.7, -187.49) * mm, "end": v(-153.85, -187.49) * mm});
            skLineSegment(sketch, "E549", {"start": v(-153.85, -187.49) * mm, "end": v(-153.85, -195.09) * mm});
            skLineSegment(sketch, "E550", {"start": v(-153.85, -195.09) * mm, "end": v(-143.03, -195.09) * mm});
            skLineSegment(sketch, "E551", {"start": v(-143.03, -195.09) * mm, "end": v(-143.03, -197.11) * mm});
            skLineSegment(sketch, "E552", {"start": v(-30.03, -197.02) * mm, "end": v(-43.04, -197.02) * mm});
            skLineSegment(sketch, "E553", {"start": v(-43.04, -197.02) * mm, "end": v(-43.04, -175.87) * mm});
            skLineSegment(sketch, "E554", {"start": v(-43.04, -175.87) * mm, "end": v(-30.1, -175.87) * mm});
            skLineSegment(sketch, "E555", {"start": v(-30.1, -175.87) * mm, "end": v(-30.1, -177.9) * mm});
            skLineSegment(sketch, "E556", {"start": v(-30.1, -177.9) * mm, "end": v(-40.85, -177.9) * mm});
            skLineSegment(sketch, "E557", {"start": v(-40.85, -177.9) * mm, "end": v(-40.85, -185.43) * mm});
            skLineSegment(sketch, "E558", {"start": v(-40.85, -185.43) * mm, "end": v(-31.69, -185.43) * mm});
            skLineSegment(sketch, "E559", {"start": v(-31.69, -185.43) * mm, "end": v(-31.69, -187.4) * mm});
            skLineSegment(sketch, "E560", {"start": v(-31.69, -187.4) * mm, "end": v(-40.85, -187.4) * mm});
            skLineSegment(sketch, "E561", {"start": v(-40.85, -187.4) * mm, "end": v(-40.85, -195) * mm});
            skLineSegment(sketch, "E562", {"start": v(-40.85, -195) * mm, "end": v(-30.03, -195) * mm});
            skLineSegment(sketch, "E563", {"start": v(-30.03, -195) * mm, "end": v(-30.03, -197.02) * mm});
            skLineSegment(sketch, "E564", {"start": v(181.62, 51) * mm, "end": v(181.62, 72.14) * mm});
            skLineSegment(sketch, "E565", {"start": v(181.62, 72.14) * mm, "end": v(183.77, 72.14) * mm});
            skLineSegment(sketch, "E566", {"start": v(183.77, 72.14) * mm, "end": v(183.77, 62.57) * mm});
            skLineSegment(sketch, "E567", {"start": v(183.77, 62.57) * mm, "end": v(193.87, 62.57) * mm});
            skLineSegment(sketch, "E568", {"start": v(193.87, 62.57) * mm, "end": v(193.87, 72.14) * mm});
            skLineSegment(sketch, "E569", {"start": v(193.87, 72.14) * mm, "end": v(196, 72.14) * mm});
            skLineSegment(sketch, "E570", {"start": v(196, 72.14) * mm, "end": v(196, 51) * mm});
            skLineSegment(sketch, "E571", {"start": v(196, 51) * mm, "end": v(193.87, 51) * mm});
            skLineSegment(sketch, "E572", {"start": v(193.87, 51) * mm, "end": v(193.87, 60.68) * mm});
            skLineSegment(sketch, "E573", {"start": v(193.87, 60.68) * mm, "end": v(183.77, 60.68) * mm});
            skLineSegment(sketch, "E574", {"start": v(183.77, 60.68) * mm, "end": v(183.77, 51) * mm});
            skLineSegment(sketch, "E575", {"start": v(183.77, 51) * mm, "end": v(181.62, 51) * mm});
            skLineSegment(sketch, "E576", {"start": v(-82.3, -114.44) * mm, "end": v(-82.3, -93.3) * mm});
            skLineSegment(sketch, "E577", {"start": v(-82.3, -93.3) * mm, "end": v(-80.15, -93.3) * mm});
            skLineSegment(sketch, "E578", {"start": v(-80.15, -93.3) * mm, "end": v(-80.15, -102.86) * mm});
            skLineSegment(sketch, "E579", {"start": v(-80.15, -102.86) * mm, "end": v(-70.05, -102.86) * mm});
            skLineSegment(sketch, "E580", {"start": v(-70.05, -102.86) * mm, "end": v(-70.05, -93.3) * mm});
            skLineSegment(sketch, "E581", {"start": v(-70.05, -93.3) * mm, "end": v(-67.92, -93.3) * mm});
            skLineSegment(sketch, "E582", {"start": v(-67.92, -93.3) * mm, "end": v(-67.92, -114.44) * mm});
            skLineSegment(sketch, "E583", {"start": v(-67.92, -114.44) * mm, "end": v(-70.05, -114.44) * mm});
            skLineSegment(sketch, "E584", {"start": v(-70.05, -114.44) * mm, "end": v(-70.05, -104.76) * mm});
            skLineSegment(sketch, "E585", {"start": v(-70.05, -104.76) * mm, "end": v(-80.15, -104.76) * mm});
            skLineSegment(sketch, "E586", {"start": v(-80.15, -104.76) * mm, "end": v(-80.15, -114.44) * mm});
            skLineSegment(sketch, "E587", {"start": v(-80.15, -114.44) * mm, "end": v(-82.3, -114.44) * mm});
            skLineSegment(sketch, "E588", {"start": v(143.94, -114.3) * mm, "end": v(143.94, -93.15) * mm});
            skLineSegment(sketch, "E589", {"start": v(143.94, -93.15) * mm, "end": v(146.1, -93.15) * mm});
            skLineSegment(sketch, "E590", {"start": v(146.1, -93.15) * mm, "end": v(146.1, -102.72) * mm});
            skLineSegment(sketch, "E591", {"start": v(146.1, -102.72) * mm, "end": v(156.19, -102.72) * mm});
            skLineSegment(sketch, "E592", {"start": v(156.19, -102.72) * mm, "end": v(156.19, -93.15) * mm});
            skLineSegment(sketch, "E593", {"start": v(156.19, -93.15) * mm, "end": v(158.32, -93.15) * mm});
            skLineSegment(sketch, "E594", {"start": v(158.32, -93.15) * mm, "end": v(158.32, -114.3) * mm});
            skLineSegment(sketch, "E595", {"start": v(158.32, -114.3) * mm, "end": v(156.19, -114.3) * mm});
            skLineSegment(sketch, "E596", {"start": v(156.19, -114.3) * mm, "end": v(156.19, -104.61) * mm});
            skLineSegment(sketch, "E597", {"start": v(156.19, -104.61) * mm, "end": v(146.1, -104.61) * mm});
            skLineSegment(sketch, "E598", {"start": v(146.1, -104.61) * mm, "end": v(146.1, -114.3) * mm});
            skLineSegment(sketch, "E599", {"start": v(146.1, -114.3) * mm, "end": v(143.94, -114.3) * mm});
            skLineSegment(sketch, "E600", {"start": v(-119.9, -197.11) * mm, "end": v(-119.9, -175.96) * mm});
            skLineSegment(sketch, "E601", {"start": v(-119.9, -175.96) * mm, "end": v(-117.75, -175.96) * mm});
            skLineSegment(sketch, "E602", {"start": v(-117.75, -175.96) * mm, "end": v(-117.75, -185.53) * mm});
            skLineSegment(sketch, "E603", {"start": v(-117.75, -185.53) * mm, "end": v(-107.65, -185.53) * mm});
            skLineSegment(sketch, "E604", {"start": v(-107.65, -185.53) * mm, "end": v(-107.65, -175.96) * mm});
            skLineSegment(sketch, "E605", {"start": v(-107.65, -175.96) * mm, "end": v(-105.52, -175.96) * mm});
            skLineSegment(sketch, "E606", {"start": v(-105.52, -175.96) * mm, "end": v(-105.52, -197.11) * mm});
            skLineSegment(sketch, "E607", {"start": v(-105.52, -197.11) * mm, "end": v(-107.65, -197.11) * mm});
            skLineSegment(sketch, "E608", {"start": v(-107.65, -197.11) * mm, "end": v(-107.65, -187.43) * mm});
            skLineSegment(sketch, "E609", {"start": v(-107.65, -187.43) * mm, "end": v(-117.75, -187.43) * mm});
            skLineSegment(sketch, "E610", {"start": v(-117.75, -187.43) * mm, "end": v(-117.75, -197.11) * mm});
            skLineSegment(sketch, "E611", {"start": v(-117.75, -197.11) * mm, "end": v(-119.9, -197.11) * mm});
            skLineSegment(sketch, "E612", {"start": v(143.95, -197.12) * mm, "end": v(143.95, -175.97) * mm});
            skLineSegment(sketch, "E613", {"start": v(143.95, -175.97) * mm, "end": v(146.11, -175.97) * mm});
            skLineSegment(sketch, "E614", {"start": v(146.11, -175.97) * mm, "end": v(146.11, -185.54) * mm});
            skLineSegment(sketch, "E615", {"start": v(146.11, -185.54) * mm, "end": v(156.2, -185.54) * mm});
            skLineSegment(sketch, "E616", {"start": v(156.2, -185.54) * mm, "end": v(156.2, -175.97) * mm});
            skLineSegment(sketch, "E617", {"start": v(156.2, -175.97) * mm, "end": v(158.34, -175.97) * mm});
            skLineSegment(sketch, "E618", {"start": v(158.34, -175.97) * mm, "end": v(158.34, -197.12) * mm});
            skLineSegment(sketch, "E619", {"start": v(158.34, -197.12) * mm, "end": v(156.2, -197.12) * mm});
            skLineSegment(sketch, "E620", {"start": v(156.2, -197.12) * mm, "end": v(156.2, -187.43) * mm});
            skLineSegment(sketch, "E621", {"start": v(156.2, -187.43) * mm, "end": v(146.11, -187.43) * mm});
            skLineSegment(sketch, "E622", {"start": v(146.11, -187.43) * mm, "end": v(146.11, -197.12) * mm});
            skLineSegment(sketch, "E623", {"start": v(146.11, -197.12) * mm, "end": v(143.95, -197.12) * mm});
            skLineSegment(sketch, "E624", {"start": v(158.8, 175.24) * mm, "end": v(158.8, 196.54) * mm});
            skLineSegment(sketch, "E625", {"start": v(158.8, 196.54) * mm, "end": v(156.63, 196.54) * mm});
            skLineSegment(sketch, "E626", {"start": v(156.63, 196.54) * mm, "end": v(156.63, 179.18) * mm});
            skLineSegment(sketch, "E627", {"start": v(156.63, 179.18) * mm, "end": v(145.52, 196.54) * mm});
            skLineSegment(sketch, "E628", {"start": v(145.52, 196.54) * mm, "end": v(143.25, 196.54) * mm});
            skLineSegment(sketch, "E629", {"start": v(143.25, 196.54) * mm, "end": v(143.25, 175.24) * mm});
            skLineSegment(sketch, "E630", {"start": v(143.25, 175.24) * mm, "end": v(145.52, 175.24) * mm});
            skLineSegment(sketch, "E631", {"start": v(145.52, 175.24) * mm, "end": v(145.52, 192.14) * mm});
            skLineSegment(sketch, "E632", {"start": v(145.52, 192.14) * mm, "end": v(156.63, 175.24) * mm});
            skLineSegment(sketch, "E633", {"start": v(156.63, 175.24) * mm, "end": v(158.8, 175.24) * mm});
            skLineSegment(sketch, "E634", {"start": v(7.97, 51.12) * mm, "end": v(7.97, 72.42) * mm});
            skLineSegment(sketch, "E635", {"start": v(7.97, 72.42) * mm, "end": v(5.8, 72.42) * mm});
            skLineSegment(sketch, "E636", {"start": v(5.8, 72.42) * mm, "end": v(5.8, 55.06) * mm});
            skLineSegment(sketch, "E637", {"start": v(5.8, 55.06) * mm, "end": v(-5.32, 72.42) * mm});
            skLineSegment(sketch, "E638", {"start": v(-5.32, 72.42) * mm, "end": v(-7.59, 72.42) * mm});
            skLineSegment(sketch, "E639", {"start": v(-7.59, 72.42) * mm, "end": v(-7.59, 51.12) * mm});
            skLineSegment(sketch, "E640", {"start": v(-7.59, 51.12) * mm, "end": v(-5.32, 51.12) * mm});
            skLineSegment(sketch, "E641", {"start": v(-5.32, 51.12) * mm, "end": v(-5.32, 68.02) * mm});
            skLineSegment(sketch, "E642", {"start": v(-5.32, 68.02) * mm, "end": v(5.8, 51.12) * mm});
            skLineSegment(sketch, "E643", {"start": v(5.8, 51.12) * mm, "end": v(7.97, 51.12) * mm});
            skLineSegment(sketch, "E644", {"start": v(83.4, 50.95) * mm, "end": v(83.4, 72.25) * mm});
            skLineSegment(sketch, "E645", {"start": v(83.4, 72.25) * mm, "end": v(81.22, 72.25) * mm});
            skLineSegment(sketch, "E646", {"start": v(81.22, 72.25) * mm, "end": v(81.22, 54.9) * mm});
            skLineSegment(sketch, "E647", {"start": v(81.22, 54.9) * mm, "end": v(70.1, 72.25) * mm});
            skLineSegment(sketch, "E648", {"start": v(70.1, 72.25) * mm, "end": v(67.83, 72.25) * mm});
            skLineSegment(sketch, "E649", {"start": v(67.83, 72.25) * mm, "end": v(67.83, 50.95) * mm});
            skLineSegment(sketch, "E650", {"start": v(67.83, 50.95) * mm, "end": v(70.1, 50.95) * mm});
            skLineSegment(sketch, "E651", {"start": v(70.1, 50.95) * mm, "end": v(70.1, 67.85) * mm});
            skLineSegment(sketch, "E652", {"start": v(70.1, 67.85) * mm, "end": v(81.22, 50.95) * mm});
            skLineSegment(sketch, "E653", {"start": v(81.22, 50.95) * mm, "end": v(83.4, 50.95) * mm});
            skLineSegment(sketch, "E654", {"start": v(158.86, 9.7) * mm, "end": v(158.86, 31) * mm});
            skLineSegment(sketch, "E655", {"start": v(158.86, 31) * mm, "end": v(156.68, 31) * mm});
            skLineSegment(sketch, "E656", {"start": v(156.68, 31) * mm, "end": v(156.68, 13.64) * mm});
            skLineSegment(sketch, "E657", {"start": v(156.68, 13.64) * mm, "end": v(145.57, 31) * mm});
            skLineSegment(sketch, "E658", {"start": v(145.57, 31) * mm, "end": v(143.3, 31) * mm});
            skLineSegment(sketch, "E659", {"start": v(143.3, 31) * mm, "end": v(143.3, 9.7) * mm});
            skLineSegment(sketch, "E660", {"start": v(143.3, 9.7) * mm, "end": v(145.57, 9.7) * mm});
            skLineSegment(sketch, "E661", {"start": v(145.57, 9.7) * mm, "end": v(145.57, 26.6) * mm});
            skLineSegment(sketch, "E662", {"start": v(145.57, 26.6) * mm, "end": v(156.68, 9.7) * mm});
            skLineSegment(sketch, "E663", {"start": v(156.68, 9.7) * mm, "end": v(158.86, 9.7) * mm});
            skLineSegment(sketch, "E664", {"start": v(-105.04, -31.7) * mm, "end": v(-105.04, -10.4) * mm});
            skLineSegment(sketch, "E665", {"start": v(-105.04, -10.4) * mm, "end": v(-107.22, -10.4) * mm});
            skLineSegment(sketch, "E666", {"start": v(-107.22, -10.4) * mm, "end": v(-107.22, -27.75) * mm});
            skLineSegment(sketch, "E667", {"start": v(-107.22, -27.75) * mm, "end": v(-118.33, -10.4) * mm});
            skLineSegment(sketch, "E668", {"start": v(-118.33, -10.4) * mm, "end": v(-120.6, -10.4) * mm});
            skLineSegment(sketch, "E669", {"start": v(-120.6, -10.4) * mm, "end": v(-120.6, -31.7) * mm});
            skLineSegment(sketch, "E670", {"start": v(-120.6, -31.7) * mm, "end": v(-118.33, -31.7) * mm});
            skLineSegment(sketch, "E671", {"start": v(-118.33, -31.7) * mm, "end": v(-118.33, -14.79) * mm});
            skLineSegment(sketch, "E672", {"start": v(-118.33, -14.79) * mm, "end": v(-107.22, -31.7) * mm});
            skLineSegment(sketch, "E673", {"start": v(-107.22, -31.7) * mm, "end": v(-105.04, -31.7) * mm});
            skLineSegment(sketch, "E674", {"start": v(8.12, -114.39) * mm, "end": v(8.12, -93.09) * mm});
            skLineSegment(sketch, "E675", {"start": v(8.12, -93.09) * mm, "end": v(5.95, -93.09) * mm});
            skLineSegment(sketch, "E676", {"start": v(5.95, -93.09) * mm, "end": v(5.95, -110.44) * mm});
            skLineSegment(sketch, "E677", {"start": v(5.95, -110.44) * mm, "end": v(-5.17, -93.09) * mm});
            skLineSegment(sketch, "E678", {"start": v(-5.17, -93.09) * mm, "end": v(-7.44, -93.09) * mm});
            skLineSegment(sketch, "E679", {"start": v(-7.44, -93.09) * mm, "end": v(-7.44, -114.39) * mm});
            skLineSegment(sketch, "E680", {"start": v(-7.44, -114.39) * mm, "end": v(-5.17, -114.39) * mm});
            skLineSegment(sketch, "E681", {"start": v(-5.17, -114.39) * mm, "end": v(-5.17, -97.48) * mm});
            skLineSegment(sketch, "E682", {"start": v(-5.17, -97.48) * mm, "end": v(5.95, -114.39) * mm});
            skLineSegment(sketch, "E683", {"start": v(5.95, -114.39) * mm, "end": v(8.12, -114.39) * mm});
            skLineSegment(sketch, "E684", {"start": v(8.11, -155.73) * mm, "end": v(8.11, -134.44) * mm});
            skLineSegment(sketch, "E685", {"start": v(8.11, -134.44) * mm, "end": v(5.94, -134.44) * mm});
            skLineSegment(sketch, "E686", {"start": v(5.94, -134.44) * mm, "end": v(5.94, -151.8) * mm});
            skLineSegment(sketch, "E687", {"start": v(5.94, -151.8) * mm, "end": v(-5.18, -134.44) * mm});
            skLineSegment(sketch, "E688", {"start": v(-5.18, -134.44) * mm, "end": v(-7.45, -134.44) * mm});
            skLineSegment(sketch, "E689", {"start": v(-7.45, -134.44) * mm, "end": v(-7.45, -155.73) * mm});
            skLineSegment(sketch, "E690", {"start": v(-7.45, -155.73) * mm, "end": v(-5.18, -155.73) * mm});
            skLineSegment(sketch, "E691", {"start": v(-5.18, -155.73) * mm, "end": v(-5.18, -138.83) * mm});
            skLineSegment(sketch, "E692", {"start": v(-5.18, -138.83) * mm, "end": v(5.94, -155.73) * mm});
            skLineSegment(sketch, "E693", {"start": v(5.94, -155.73) * mm, "end": v(8.11, -155.73) * mm});
            skLineSegment(sketch, "E694", {"start": v(-67.27, -197.21) * mm, "end": v(-67.27, -175.91) * mm});
            skLineSegment(sketch, "E695", {"start": v(-67.27, -175.91) * mm, "end": v(-69.45, -175.91) * mm});
            skLineSegment(sketch, "E696", {"start": v(-69.45, -175.91) * mm, "end": v(-69.45, -193.27) * mm});
            skLineSegment(sketch, "E697", {"start": v(-69.45, -193.27) * mm, "end": v(-80.56, -175.91) * mm});
            skLineSegment(sketch, "E698", {"start": v(-80.56, -175.91) * mm, "end": v(-82.83, -175.91) * mm});
            skLineSegment(sketch, "E699", {"start": v(-82.83, -175.91) * mm, "end": v(-82.83, -197.21) * mm});
            skLineSegment(sketch, "E700", {"start": v(-82.83, -197.21) * mm, "end": v(-80.56, -197.21) * mm});
            skLineSegment(sketch, "E701", {"start": v(-80.56, -197.21) * mm, "end": v(-80.56, -180.31) * mm});
            skLineSegment(sketch, "E702", {"start": v(-80.56, -180.31) * mm, "end": v(-69.45, -197.21) * mm});
            skLineSegment(sketch, "E703", {"start": v(-69.45, -197.21) * mm, "end": v(-67.27, -197.21) * mm});
            skLineSegment(sketch, "E704", {"start": v(45.84, -197.17) * mm, "end": v(45.84, -175.87) * mm});
            skLineSegment(sketch, "E705", {"start": v(45.84, -175.87) * mm, "end": v(43.66, -175.87) * mm});
            skLineSegment(sketch, "E706", {"start": v(43.66, -175.87) * mm, "end": v(43.66, -193.22) * mm});
            skLineSegment(sketch, "E707", {"start": v(43.66, -193.22) * mm, "end": v(32.55, -175.87) * mm});
            skLineSegment(sketch, "E708", {"start": v(32.55, -175.87) * mm, "end": v(30.28, -175.87) * mm});
            skLineSegment(sketch, "E709", {"start": v(30.28, -175.87) * mm, "end": v(30.28, -197.17) * mm});
            skLineSegment(sketch, "E710", {"start": v(30.28, -197.17) * mm, "end": v(32.55, -197.17) * mm});
            skLineSegment(sketch, "E711", {"start": v(32.55, -197.17) * mm, "end": v(32.55, -180.27) * mm});
            skLineSegment(sketch, "E712", {"start": v(32.55, -180.27) * mm, "end": v(43.66, -197.17) * mm});
            skLineSegment(sketch, "E713", {"start": v(43.66, -197.17) * mm, "end": v(45.84, -197.17) * mm});
            skLineSegment(sketch, "E714", {"start": v(120.1, -31.62) * mm, "end": v(117.86, -31.62) * mm});
            skLineSegment(sketch, "E715", {"start": v(117.86, -31.62) * mm, "end": v(113.32, -14.9) * mm});
            skLineSegment(sketch, "E716", {"start": v(113.32, -14.9) * mm, "end": v(108.7, -31.62) * mm});
            skLineSegment(sketch, "E717", {"start": v(108.7, -31.62) * mm, "end": v(106.89, -31.62) * mm});
            skLineSegment(sketch, "E718", {"start": v(106.89, -31.62) * mm, "end": v(101.56, -10.48) * mm});
            skLineSegment(sketch, "E719", {"start": v(101.56, -10.48) * mm, "end": v(103.75, -10.48) * mm});
            skLineSegment(sketch, "E720", {"start": v(103.75, -10.48) * mm, "end": v(107.76, -27.35) * mm});
            skLineSegment(sketch, "E721", {"start": v(107.76, -27.35) * mm, "end": v(112.26, -10.48) * mm});
            skLineSegment(sketch, "E722", {"start": v(112.26, -10.48) * mm, "end": v(114.42, -10.48) * mm});
            skLineSegment(sketch, "E723", {"start": v(114.42, -10.48) * mm, "end": v(118.88, -27.35) * mm});
            skLineSegment(sketch, "E724", {"start": v(118.88, -27.35) * mm, "end": v(123.16, -10.48) * mm});
            skLineSegment(sketch, "E725", {"start": v(123.16, -10.48) * mm, "end": v(125.47, -10.48) * mm});
            skLineSegment(sketch, "E726", {"start": v(125.47, -10.48) * mm, "end": v(120.1, -31.62) * mm});
            skLineSegment(sketch, "E727", {"start": v(82.44, -155.58) * mm, "end": v(80.2, -155.58) * mm});
            skLineSegment(sketch, "E728", {"start": v(80.2, -155.58) * mm, "end": v(75.66, -138.87) * mm});
            skLineSegment(sketch, "E729", {"start": v(75.66, -138.87) * mm, "end": v(71.05, -155.58) * mm});
            skLineSegment(sketch, "E730", {"start": v(71.05, -155.58) * mm, "end": v(69.23, -155.58) * mm});
            skLineSegment(sketch, "E731", {"start": v(69.23, -155.58) * mm, "end": v(63.9, -134.44) * mm});
            skLineSegment(sketch, "E732", {"start": v(63.9, -134.44) * mm, "end": v(66.1, -134.44) * mm});
            skLineSegment(sketch, "E733", {"start": v(66.1, -134.44) * mm, "end": v(70.1, -151.31) * mm});
            skLineSegment(sketch, "E734", {"start": v(70.1, -151.31) * mm, "end": v(74.6, -134.44) * mm});
            skLineSegment(sketch, "E735", {"start": v(74.6, -134.44) * mm, "end": v(76.76, -134.44) * mm});
            skLineSegment(sketch, "E736", {"start": v(76.76, -134.44) * mm, "end": v(81.22, -151.31) * mm});
            skLineSegment(sketch, "E737", {"start": v(81.22, -151.31) * mm, "end": v(85.5, -134.44) * mm});
            skLineSegment(sketch, "E738", {"start": v(85.5, -134.44) * mm, "end": v(87.8, -134.44) * mm});
            skLineSegment(sketch, "E739", {"start": v(87.8, -134.44) * mm, "end": v(82.44, -155.58) * mm});
            skLineSegment(sketch, "E740", {"start": v(37.18, 180.1) * mm, "end": v(37.18, 182.25) * mm});
            skLineSegment(sketch, "E741", {"start": v(37.18, 182.25) * mm, "end": v(41.69, 182.25) * mm});
            skLineSegment(sketch, "E742", {"start": v(37.18, 180.1) * mm, "end": v(42.48, 180.1) * mm});
            skLineSegment(sketch, "E743", {"start": v(46.68, 175.05) * mm, "end": v(44.26, 175.05) * mm});
            skLineSegment(sketch, "E744", {"start": v(44.26, 175.05) * mm, "end": v(42.48, 180.1) * mm});
            skLineSegment(sketch, "E745", {"start": v(38.1, 192.7) * mm, "end": v(31.77, 175.05) * mm});
            skLineSegment(sketch, "E746", {"start": v(31.77, 175.05) * mm, "end": v(29.28, 175.05) * mm});
            skLineSegment(sketch, "E747", {"start": v(29.28, 175.05) * mm, "end": v(37.14, 196.21) * mm});
            skLineSegment(sketch, "E748", {"start": v(37.14, 196.21) * mm, "end": v(38.85, 196.21) * mm});
            skLineSegment(sketch, "E749", {"start": v(38.85, 196.21) * mm, "end": v(46.68, 175.05) * mm});
            skLineSegment(sketch, "E750", {"start": v(41.69, 182.25) * mm, "end": v(38.1, 192.7) * mm});
            skLineSegment(sketch, "E751", {"start": v(112.57, 57.06) * mm, "end": v(112.57, 59.22) * mm});
            skLineSegment(sketch, "E752", {"start": v(112.57, 59.22) * mm, "end": v(117.07, 59.22) * mm});
            skLineSegment(sketch, "E753", {"start": v(112.57, 57.06) * mm, "end": v(117.87, 57.07) * mm});
            skLineSegment(sketch, "E754", {"start": v(122.06, 52.02) * mm, "end": v(119.64, 52.02) * mm});
            skLineSegment(sketch, "E755", {"start": v(119.64, 52.02) * mm, "end": v(117.87, 57.07) * mm});
            skLineSegment(sketch, "E756", {"start": v(113.48, 69.66) * mm, "end": v(107.16, 52.02) * mm});
            skLineSegment(sketch, "E757", {"start": v(107.16, 52.02) * mm, "end": v(104.66, 52.02) * mm});
            skLineSegment(sketch, "E758", {"start": v(104.66, 52.02) * mm, "end": v(112.53, 73.17) * mm});
            skLineSegment(sketch, "E759", {"start": v(112.53, 73.17) * mm, "end": v(114.23, 73.17) * mm});
            skLineSegment(sketch, "E760", {"start": v(114.23, 73.17) * mm, "end": v(122.06, 52.02) * mm});
            skLineSegment(sketch, "E761", {"start": v(117.07, 59.22) * mm, "end": v(113.48, 69.66) * mm});
            skLineSegment(sketch, "E762", {"start": v(-38.2, 14.72) * mm, "end": v(-38.2, 16.88) * mm});
            skLineSegment(sketch, "E763", {"start": v(-38.2, 16.88) * mm, "end": v(-33.69, 16.88) * mm});
            skLineSegment(sketch, "E764", {"start": v(-38.2, 14.72) * mm, "end": v(-32.9, 14.73) * mm});
            skLineSegment(sketch, "E765", {"start": v(-28.7, 9.68) * mm, "end": v(-31.12, 9.68) * mm});
            skLineSegment(sketch, "E766", {"start": v(-31.12, 9.68) * mm, "end": v(-32.9, 14.73) * mm});
            skLineSegment(sketch, "E767", {"start": v(-37.28, 27.32) * mm, "end": v(-43.6, 9.68) * mm});
            skLineSegment(sketch, "E768", {"start": v(-43.6, 9.68) * mm, "end": v(-46.1, 9.68) * mm});
            skLineSegment(sketch, "E769", {"start": v(-46.1, 9.68) * mm, "end": v(-38.23, 30.84) * mm});
            skLineSegment(sketch, "E770", {"start": v(-38.23, 30.84) * mm, "end": v(-36.53, 30.84) * mm});
            skLineSegment(sketch, "E771", {"start": v(-36.53, 30.84) * mm, "end": v(-28.7, 9.68) * mm});
            skLineSegment(sketch, "E772", {"start": v(-33.69, 16.88) * mm, "end": v(-37.28, 27.32) * mm});
            skLineSegment(sketch, "E773", {"start": v(-0.42, -26.69) * mm, "end": v(-0.42, -24.53) * mm});
            skLineSegment(sketch, "E774", {"start": v(-0.42, -24.53) * mm, "end": v(4.08, -24.53) * mm});
            skLineSegment(sketch, "E775", {"start": v(-0.42, -26.69) * mm, "end": v(4.88, -26.68) * mm});
            skLineSegment(sketch, "E776", {"start": v(9.07, -31.73) * mm, "end": v(6.65, -31.73) * mm});
            skLineSegment(sketch, "E777", {"start": v(6.65, -31.73) * mm, "end": v(4.88, -26.68) * mm});
            skLineSegment(sketch, "E778", {"start": v(0.49, -14.09) * mm, "end": v(-5.83, -31.73) * mm});
            skLineSegment(sketch, "E779", {"start": v(-5.83, -31.73) * mm, "end": v(-8.33, -31.73) * mm});
            skLineSegment(sketch, "E780", {"start": v(-8.33, -31.73) * mm, "end": v(-0.46, -10.57) * mm});
            skLineSegment(sketch, "E781", {"start": v(-0.46, -10.57) * mm, "end": v(1.24, -10.57) * mm});
            skLineSegment(sketch, "E782", {"start": v(1.24, -10.57) * mm, "end": v(9.07, -31.73) * mm});
            skLineSegment(sketch, "E783", {"start": v(4.08, -24.53) * mm, "end": v(0.49, -14.09) * mm});
            skLineSegment(sketch, "E784", {"start": v(74.82, -109.4) * mm, "end": v(74.82, -107.24) * mm});
            skLineSegment(sketch, "E785", {"start": v(74.82, -107.24) * mm, "end": v(79.32, -107.24) * mm});
            skLineSegment(sketch, "E786", {"start": v(74.82, -109.4) * mm, "end": v(80.11, -109.39) * mm});
            skLineSegment(sketch, "E787", {"start": v(84.31, -114.44) * mm, "end": v(81.9, -114.44) * mm});
            skLineSegment(sketch, "E788", {"start": v(81.9, -114.44) * mm, "end": v(80.11, -109.39) * mm});
            skLineSegment(sketch, "E789", {"start": v(75.72, -96.8) * mm, "end": v(69.4, -114.44) * mm});
            skLineSegment(sketch, "E790", {"start": v(69.4, -114.44) * mm, "end": v(66.9, -114.44) * mm});
            skLineSegment(sketch, "E791", {"start": v(66.9, -114.44) * mm, "end": v(74.78, -93.28) * mm});
            skLineSegment(sketch, "E792", {"start": v(74.78, -93.28) * mm, "end": v(76.48, -93.28) * mm});
            skLineSegment(sketch, "E793", {"start": v(76.48, -93.28) * mm, "end": v(84.31, -114.44) * mm});
            skLineSegment(sketch, "E794", {"start": v(79.32, -107.24) * mm, "end": v(75.72, -96.8) * mm});
            skLineSegment(sketch, "E795", {"start": v(-76.29, 175.03) * mm, "end": v(-76.29, 196.29) * mm});
            skLineSegment(sketch, "E796", {"start": v(-76.29, 196.29) * mm, "end": v(-73.9, 196.29) * mm});
            skLineSegment(sketch, "E797", {"start": v(-73.9, 196.29) * mm, "end": v(-73.9, 175.03) * mm});
            skLineSegment(sketch, "E798", {"start": v(-73.9, 175.03) * mm, "end": v(-76.29, 175.03) * mm});
            skLineSegment(sketch, "E799", {"start": v(-76.27, 92.23) * mm, "end": v(-76.27, 113.49) * mm});
            skLineSegment(sketch, "E800", {"start": v(-76.27, 113.49) * mm, "end": v(-73.9, 113.49) * mm});
            skLineSegment(sketch, "E801", {"start": v(-73.9, 113.49) * mm, "end": v(-73.9, 92.23) * mm});
            skLineSegment(sketch, "E802", {"start": v(-73.9, 92.23) * mm, "end": v(-76.27, 92.23) * mm});
            skLineSegment(sketch, "E803", {"start": v(-0.85, 92.2) * mm, "end": v(-0.85, 113.47) * mm});
            skLineSegment(sketch, "E804", {"start": v(-0.85, 113.47) * mm, "end": v(1.54, 113.47) * mm});
            skLineSegment(sketch, "E805", {"start": v(1.54, 113.47) * mm, "end": v(1.54, 92.2) * mm});
            skLineSegment(sketch, "E806", {"start": v(1.54, 92.2) * mm, "end": v(-0.85, 92.2) * mm});
            skLineSegment(sketch, "E807", {"start": v(-151.67, -31.69) * mm, "end": v(-151.67, -10.43) * mm});
            skLineSegment(sketch, "E808", {"start": v(-151.67, -10.43) * mm, "end": v(-149.29, -10.43) * mm});
            skLineSegment(sketch, "E809", {"start": v(-149.29, -10.43) * mm, "end": v(-149.29, -31.69) * mm});
            skLineSegment(sketch, "E810", {"start": v(-149.29, -31.69) * mm, "end": v(-151.67, -31.69) * mm});
            skLineSegment(sketch, "E811", {"start": v(187.6, -31.7) * mm, "end": v(187.6, -10.45) * mm});
            skLineSegment(sketch, "E812", {"start": v(187.6, -10.45) * mm, "end": v(189.98, -10.45) * mm});
            skLineSegment(sketch, "E813", {"start": v(189.98, -10.45) * mm, "end": v(189.98, -31.7) * mm});
            skLineSegment(sketch, "E814", {"start": v(189.98, -31.7) * mm, "end": v(187.6, -31.7) * mm});
            skLineSegment(sketch, "E815", {"start": v(-76.28, -72.99) * mm, "end": v(-76.28, -51.73) * mm});
            skLineSegment(sketch, "E816", {"start": v(-76.28, -51.73) * mm, "end": v(-73.9, -51.73) * mm});
            skLineSegment(sketch, "E817", {"start": v(-73.9, -51.73) * mm, "end": v(-73.9, -72.99) * mm});
            skLineSegment(sketch, "E818", {"start": v(-73.9, -72.99) * mm, "end": v(-76.28, -72.99) * mm});
            skLineSegment(sketch, "E819", {"start": v(112.24, -73.01) * mm, "end": v(112.24, -51.75) * mm});
            skLineSegment(sketch, "E820", {"start": v(112.24, -51.75) * mm, "end": v(114.63, -51.75) * mm});
            skLineSegment(sketch, "E821", {"start": v(114.63, -51.75) * mm, "end": v(114.63, -73.01) * mm});
            skLineSegment(sketch, "E822", {"start": v(114.63, -73.01) * mm, "end": v(112.24, -73.01) * mm});
            skLineSegment(sketch, "E823", {"start": v(-151.56, -155.78) * mm, "end": v(-151.56, -134.52) * mm});
            skLineSegment(sketch, "E824", {"start": v(-151.56, -134.52) * mm, "end": v(-149.18, -134.52) * mm});
            skLineSegment(sketch, "E825", {"start": v(-149.18, -134.52) * mm, "end": v(-149.18, -155.78) * mm});
            skLineSegment(sketch, "E826", {"start": v(-149.18, -155.78) * mm, "end": v(-151.56, -155.78) * mm});
            skLineSegment(sketch, "E827", {"start": v(-195.34, 9.74) * mm, "end": v(-195.34, 30.89) * mm});
            skLineSegment(sketch, "E828", {"start": v(-195.34, 30.89) * mm, "end": v(-193.18, 30.89) * mm});
            skLineSegment(sketch, "E829", {"start": v(-193.18, 30.89) * mm, "end": v(-193.18, 21.32) * mm});
            skLineSegment(sketch, "E830", {"start": v(-193.18, 21.32) * mm, "end": v(-183.09, 21.32) * mm});
            skLineSegment(sketch, "E831", {"start": v(-183.09, 21.32) * mm, "end": v(-183.09, 30.89) * mm});
            skLineSegment(sketch, "E832", {"start": v(-183.09, 30.89) * mm, "end": v(-180.95, 30.89) * mm});
            skLineSegment(sketch, "E833", {"start": v(-180.95, 30.89) * mm, "end": v(-180.95, 9.74) * mm});
            skLineSegment(sketch, "E834", {"start": v(-180.95, 9.74) * mm, "end": v(-183.09, 9.74) * mm});
            skLineSegment(sketch, "E835", {"start": v(-183.09, 9.74) * mm, "end": v(-183.09, 19.42) * mm});
            skLineSegment(sketch, "E836", {"start": v(-183.09, 19.42) * mm, "end": v(-193.18, 19.42) * mm});
            skLineSegment(sketch, "E837", {"start": v(-193.18, 19.42) * mm, "end": v(-193.18, 9.74) * mm});
            skLineSegment(sketch, "E838", {"start": v(-193.18, 9.74) * mm, "end": v(-195.34, 9.74) * mm});
            skLineSegment(sketch, "E839", {"start": v(-151.27, 14.81) * mm, "end": v(-151.27, 16.97) * mm});
            skLineSegment(sketch, "E840", {"start": v(-151.27, 16.97) * mm, "end": v(-146.77, 16.97) * mm});
            skLineSegment(sketch, "E841", {"start": v(-151.27, 14.81) * mm, "end": v(-145.98, 14.82) * mm});
            skLineSegment(sketch, "E842", {"start": v(-141.78, 9.77) * mm, "end": v(-144.2, 9.77) * mm});
            skLineSegment(sketch, "E843", {"start": v(-144.2, 9.77) * mm, "end": v(-145.98, 14.82) * mm});
            skLineSegment(sketch, "E844", {"start": v(-150.37, 27.41) * mm, "end": v(-156.68, 9.77) * mm});
            skLineSegment(sketch, "E845", {"start": v(-156.68, 9.77) * mm, "end": v(-159.18, 9.77) * mm});
            skLineSegment(sketch, "E846", {"start": v(-159.18, 9.77) * mm, "end": v(-151.31, 30.93) * mm});
            skLineSegment(sketch, "E847", {"start": v(-151.31, 30.93) * mm, "end": v(-149.6, 30.93) * mm});
            skLineSegment(sketch, "E848", {"start": v(-149.6, 30.93) * mm, "end": v(-141.78, 9.77) * mm});
            skLineSegment(sketch, "E849", {"start": v(-146.77, 16.97) * mm, "end": v(-150.37, 27.41) * mm});
            skLineSegment(sketch, "E850", {"start": v(-195.02, -65.52) * mm, "end": v(-195.02, -52.01) * mm});
            skLineSegment(sketch, "E851", {"start": v(-195.02, -52.01) * mm, "end": v(-186.96, -52.01) * mm});
            skLineSegment(sketch, "E852", {"start": v(-195.02, -65.52) * mm, "end": v(-192.79, -65.52) * mm});
            skLineSegment(sketch, "E853", {"start": v(-192.79, -65.52) * mm, "end": v(-192.79, -53.83) * mm});
            skLineSegment(sketch, "E854", {"start": v(-192.79, -53.83) * mm, "end": v(-187.09, -53.83) * mm});
            skArc(sketch, "E855", {"start": v(-180.53, -58.67) * mm, "mid": v(-182.4, -54.05) * mm, "end": v(-186.96, -52.01) * mm});
            skArc(sketch, "E856", {"start": v(-182.57, -57.84) * mm, "mid": v(-184.12, -55.04) * mm, "end": v(-187.09, -53.83) * mm});
            skLineSegment(sketch, "E857", {"start": v(-182.57, -57.84) * mm, "end": v(-182.57, -66.54) * mm});
            skLineSegment(sketch, "E858", {"start": v(-180.53, -58.67) * mm, "end": v(-180.53, -66.5) * mm});
            skLineSegment(sketch, "E859", {"start": v(-195.02, -71) * mm, "end": v(-195.02, -73.05) * mm});
            skLineSegment(sketch, "E860", {"start": v(-195.02, -73.05) * mm, "end": v(-187.75, -73.05) * mm});
            skLineSegment(sketch, "E861", {"start": v(-195.02, -71) * mm, "end": v(-187.2, -71) * mm});
            skArc(sketch, "E862", {"start": v(-187.2, -71) * mm, "mid": v(-184.05, -69.64) * mm, "end": v(-182.57, -66.54) * mm});
            skArc(sketch, "E863", {"start": v(-187.75, -73.05) * mm, "mid": v(-182.72, -71.34) * mm, "end": v(-180.53, -66.5) * mm});
            skLineSegment(sketch, "E864", {"start": v(69.06, 92.36) * mm, "end": v(69.06, 104.04) * mm});
            skLineSegment(sketch, "E865", {"start": v(69.06, 104.04) * mm, "end": v(77.66, 104.04) * mm});
            skLineSegment(sketch, "E866", {"start": v(69.06, 92.36) * mm, "end": v(71.28, 92.36) * mm});
            skLineSegment(sketch, "E867", {"start": v(71.28, 92.36) * mm, "end": v(71.28, 102) * mm});
            skLineSegment(sketch, "E868", {"start": v(71.28, 102) * mm, "end": v(76.25, 102) * mm});
            skLineSegment(sketch, "E869", {"start": v(76.25, 102) * mm, "end": v(81.5, 92.36) * mm});
            skLineSegment(sketch, "E870", {"start": v(81.5, 92.36) * mm, "end": v(83.86, 92.36) * mm});
            skLineSegment(sketch, "E871", {"start": v(83.86, 92.36) * mm, "end": v(78.8, 102) * mm});
            skLineSegment(sketch, "E872", {"start": v(69.06, 111.56) * mm, "end": v(69.06, 113.64) * mm});
            skLineSegment(sketch, "E873", {"start": v(69.06, 113.64) * mm, "end": v(77.66, 113.64) * mm});
            skLineSegment(sketch, "E874", {"start": v(69.06, 111.56) * mm, "end": v(77.66, 111.56) * mm});
            skArc(sketch, "E875", {"start": v(77.66, 104.04) * mm, "mid": v(81.3, 107.8) * mm, "end": v(77.66, 111.56) * mm});
            skArc(sketch, "E876", {"start": v(78.8, 102) * mm, "mid": v(83.5, 108.34) * mm, "end": v(77.66, 113.64) * mm});
            skLineSegment(sketch, "E877", {"start": v(-119.47, 50.86) * mm, "end": v(-119.47, 62.54) * mm});
            skLineSegment(sketch, "E878", {"start": v(-119.47, 62.54) * mm, "end": v(-110.86, 62.54) * mm});
            skLineSegment(sketch, "E879", {"start": v(-119.47, 50.86) * mm, "end": v(-117.25, 50.86) * mm});
            skLineSegment(sketch, "E880", {"start": v(-117.25, 50.86) * mm, "end": v(-117.25, 60.5) * mm});
            skLineSegment(sketch, "E881", {"start": v(-117.25, 60.5) * mm, "end": v(-112.28, 60.5) * mm});
            skLineSegment(sketch, "E882", {"start": v(-112.28, 60.5) * mm, "end": v(-107.03, 50.86) * mm});
            skLineSegment(sketch, "E883", {"start": v(-107.03, 50.86) * mm, "end": v(-104.67, 50.86) * mm});
            skLineSegment(sketch, "E884", {"start": v(-104.67, 50.86) * mm, "end": v(-109.73, 60.5) * mm});
            skLineSegment(sketch, "E885", {"start": v(-119.47, 70.06) * mm, "end": v(-119.47, 72.14) * mm});
            skLineSegment(sketch, "E886", {"start": v(-119.47, 72.14) * mm, "end": v(-110.86, 72.14) * mm});
            skLineSegment(sketch, "E887", {"start": v(-119.47, 70.06) * mm, "end": v(-110.86, 70.06) * mm});
            skArc(sketch, "E888", {"start": v(-110.86, 62.54) * mm, "mid": v(-107.22, 66.3) * mm, "end": v(-110.86, 70.06) * mm});
            skArc(sketch, "E889", {"start": v(-109.73, 60.5) * mm, "mid": v(-105.03, 66.83) * mm, "end": v(-110.86, 72.14) * mm});
            skLineSegment(sketch, "E890", {"start": v(-157.12, -73.1) * mm, "end": v(-157.12, -61.42) * mm});
            skLineSegment(sketch, "E891", {"start": v(-157.12, -61.42) * mm, "end": v(-148.52, -61.42) * mm});
            skLineSegment(sketch, "E892", {"start": v(-157.12, -73.1) * mm, "end": v(-154.9, -73.1) * mm});
            skLineSegment(sketch, "E893", {"start": v(-154.9, -73.1) * mm, "end": v(-154.9, -63.45) * mm});
            skLineSegment(sketch, "E894", {"start": v(-154.9, -63.45) * mm, "end": v(-149.93, -63.45) * mm});
            skLineSegment(sketch, "E895", {"start": v(-149.93, -63.45) * mm, "end": v(-144.68, -73.1) * mm});
            skLineSegment(sketch, "E896", {"start": v(-144.68, -73.1) * mm, "end": v(-142.32, -73.1) * mm});
            skLineSegment(sketch, "E897", {"start": v(-142.32, -73.1) * mm, "end": v(-147.38, -63.45) * mm});
            skLineSegment(sketch, "E898", {"start": v(-157.12, -53.9) * mm, "end": v(-157.12, -51.82) * mm});
            skLineSegment(sketch, "E899", {"start": v(-157.12, -51.82) * mm, "end": v(-148.52, -51.82) * mm});
            skLineSegment(sketch, "E900", {"start": v(-157.12, -53.9) * mm, "end": v(-148.52, -53.9) * mm});
            skArc(sketch, "E901", {"start": v(-148.52, -61.42) * mm, "mid": v(-144.87, -57.66) * mm, "end": v(-148.52, -53.9) * mm});
            skArc(sketch, "E902", {"start": v(-147.38, -63.45) * mm, "mid": v(-142.68, -57.12) * mm, "end": v(-148.52, -51.82) * mm});
            skLineSegment(sketch, "E903", {"start": v(182.13, -73.13) * mm, "end": v(182.13, -61.45) * mm});
            skLineSegment(sketch, "E904", {"start": v(182.13, -61.45) * mm, "end": v(190.74, -61.45) * mm});
            skLineSegment(sketch, "E905", {"start": v(182.13, -73.13) * mm, "end": v(184.35, -73.13) * mm});
            skLineSegment(sketch, "E906", {"start": v(184.35, -73.13) * mm, "end": v(184.35, -63.49) * mm});
            skLineSegment(sketch, "E907", {"start": v(184.35, -63.49) * mm, "end": v(189.32, -63.49) * mm});
            skLineSegment(sketch, "E908", {"start": v(189.32, -63.49) * mm, "end": v(194.57, -73.13) * mm});
            skLineSegment(sketch, "E909", {"start": v(194.57, -73.13) * mm, "end": v(196.93, -73.13) * mm});
            skLineSegment(sketch, "E910", {"start": v(196.93, -73.13) * mm, "end": v(191.87, -63.49) * mm});
            skLineSegment(sketch, "E911", {"start": v(182.13, -53.93) * mm, "end": v(182.13, -51.85) * mm});
            skLineSegment(sketch, "E912", {"start": v(182.13, -51.85) * mm, "end": v(190.74, -51.85) * mm});
            skLineSegment(sketch, "E913", {"start": v(182.13, -53.93) * mm, "end": v(190.74, -53.93) * mm});
            skArc(sketch, "E914", {"start": v(190.74, -61.45) * mm, "mid": v(194.38, -57.7) * mm, "end": v(190.74, -53.93) * mm});
            skArc(sketch, "E915", {"start": v(191.87, -63.49) * mm, "mid": v(196.57, -57.16) * mm, "end": v(190.74, -51.85) * mm});
            skLineSegment(sketch, "E916", {"start": v(182.1, -197.38) * mm, "end": v(182.1, -185.7) * mm});
            skLineSegment(sketch, "E917", {"start": v(182.1, -185.7) * mm, "end": v(190.7, -185.7) * mm});
            skLineSegment(sketch, "E918", {"start": v(182.1, -197.38) * mm, "end": v(184.33, -197.38) * mm});
            skLineSegment(sketch, "E919", {"start": v(184.33, -197.38) * mm, "end": v(184.33, -187.73) * mm});
            skLineSegment(sketch, "E920", {"start": v(184.33, -187.73) * mm, "end": v(189.3, -187.73) * mm});
            skLineSegment(sketch, "E921", {"start": v(189.3, -187.73) * mm, "end": v(194.54, -197.38) * mm});
            skLineSegment(sketch, "E922", {"start": v(194.54, -197.38) * mm, "end": v(196.9, -197.38) * mm});
            skLineSegment(sketch, "E923", {"start": v(196.9, -197.38) * mm, "end": v(191.84, -187.73) * mm});
            skLineSegment(sketch, "E924", {"start": v(182.1, -178.18) * mm, "end": v(182.1, -176.1) * mm});
            skLineSegment(sketch, "E925", {"start": v(182.1, -176.1) * mm, "end": v(190.7, -176.1) * mm});
            skLineSegment(sketch, "E926", {"start": v(182.1, -178.18) * mm, "end": v(190.7, -178.18) * mm});
            skArc(sketch, "E927", {"start": v(190.71, -185.7) * mm, "mid": v(194.35, -181.94) * mm, "end": v(190.71, -178.18) * mm});
            skArc(sketch, "E928", {"start": v(191.85, -187.73) * mm, "mid": v(196.55, -181.4) * mm, "end": v(190.7, -176.1) * mm});
            skLineSegment(sketch, "E929", {"start": v(-80.5, 72.22) * mm, "end": v(-80.5, 50.88) * mm});
            skLineSegment(sketch, "E930", {"start": v(-80.5, 50.88) * mm, "end": v(-78.23, 50.88) * mm});
            skLineSegment(sketch, "E931", {"start": v(-78.23, 50.88) * mm, "end": v(-78.23, 60.26) * mm});
            skLineSegment(sketch, "E932", {"start": v(-78.23, 60.26) * mm, "end": v(-69.12, 60.26) * mm});
            skLineSegment(sketch, "E933", {"start": v(-69.12, 60.26) * mm, "end": v(-69.12, 62.15) * mm});
            skLineSegment(sketch, "E934", {"start": v(-69.12, 62.15) * mm, "end": v(-78.23, 62.15) * mm});
            skLineSegment(sketch, "E935", {"start": v(-78.23, 62.15) * mm, "end": v(-78.23, 70.1) * mm});
            skLineSegment(sketch, "E936", {"start": v(-78.23, 70.1) * mm, "end": v(-67.57, 70.1) * mm});
            skLineSegment(sketch, "E937", {"start": v(-67.57, 70.1) * mm, "end": v(-67.57, 72.22) * mm});
            skLineSegment(sketch, "E938", {"start": v(-67.57, 72.22) * mm, "end": v(-80.5, 72.22) * mm});
            skLineSegment(sketch, "E939", {"start": v(183.38, -134.58) * mm, "end": v(183.38, -155.92) * mm});
            skLineSegment(sketch, "E940", {"start": v(183.38, -155.92) * mm, "end": v(185.65, -155.92) * mm});
            skLineSegment(sketch, "E941", {"start": v(185.65, -155.92) * mm, "end": v(185.65, -146.53) * mm});
            skLineSegment(sketch, "E942", {"start": v(185.65, -146.53) * mm, "end": v(194.76, -146.53) * mm});
            skLineSegment(sketch, "E943", {"start": v(194.76, -146.53) * mm, "end": v(194.76, -144.64) * mm});
            skLineSegment(sketch, "E944", {"start": v(194.76, -144.64) * mm, "end": v(185.65, -144.64) * mm});
            skLineSegment(sketch, "E945", {"start": v(185.65, -144.64) * mm, "end": v(185.65, -136.7) * mm});
            skLineSegment(sketch, "E946", {"start": v(185.65, -136.7) * mm, "end": v(196.32, -136.7) * mm});
            skLineSegment(sketch, "E947", {"start": v(196.32, -136.7) * mm, "end": v(196.32, -134.58) * mm});
            skLineSegment(sketch, "E948", {"start": v(196.32, -134.58) * mm, "end": v(183.38, -134.58) * mm});
            skLineSegment(sketch, "E949", {"start": v(-189.26, 51.1) * mm, "end": v(-196.03, 72.09) * mm});
            skLineSegment(sketch, "E950", {"start": v(-196.03, 72.09) * mm, "end": v(-193.57, 72.09) * mm});
            skLineSegment(sketch, "E951", {"start": v(-193.57, 72.09) * mm, "end": v(-188.16, 55.33) * mm});
            skLineSegment(sketch, "E952", {"start": v(-188.16, 55.33) * mm, "end": v(-182.72, 72.09) * mm});
            skLineSegment(sketch, "E953", {"start": v(-182.72, 72.09) * mm, "end": v(-180.37, 72.09) * mm});
            skLineSegment(sketch, "E954", {"start": v(-180.37, 72.09) * mm, "end": v(-187.33, 51.1) * mm});
            skLineSegment(sketch, "E955", {"start": v(-187.33, 51.1) * mm, "end": v(-189.26, 51.1) * mm});
            skLineSegment(sketch, "E956", {"start": v(74.75, -72.92) * mm, "end": v(67.98, -51.92) * mm});
            skLineSegment(sketch, "E957", {"start": v(67.98, -51.92) * mm, "end": v(70.44, -51.92) * mm});
            skLineSegment(sketch, "E958", {"start": v(70.44, -51.92) * mm, "end": v(75.85, -68.68) * mm});
            skLineSegment(sketch, "E959", {"start": v(75.85, -68.68) * mm, "end": v(81.3, -51.92) * mm});
            skLineSegment(sketch, "E960", {"start": v(81.3, -51.92) * mm, "end": v(83.64, -51.92) * mm});
            skLineSegment(sketch, "E961", {"start": v(83.64, -51.92) * mm, "end": v(76.68, -72.92) * mm});
            skLineSegment(sketch, "E962", {"start": v(76.68, -72.92) * mm, "end": v(74.75, -72.92) * mm});
            skLineSegment(sketch, "E963", {"start": v(-8.63, -72.95) * mm, "end": v(-8.63, -51.91) * mm});
            skLineSegment(sketch, "E964", {"start": v(-8.63, -51.91) * mm, "end": v(-6.58, -51.91) * mm});
            skLineSegment(sketch, "E965", {"start": v(-6.58, -51.91) * mm, "end": v(0.34, -67.54) * mm});
            skLineSegment(sketch, "E966", {"start": v(0.34, -67.54) * mm, "end": v(7.15, -51.91) * mm});
            skLineSegment(sketch, "E967", {"start": v(7.15, -51.91) * mm, "end": v(9.04, -51.91) * mm});
            skLineSegment(sketch, "E968", {"start": v(9.04, -51.91) * mm, "end": v(9.04, -72.95) * mm});
            skLineSegment(sketch, "E969", {"start": v(9.04, -72.95) * mm, "end": v(7.15, -72.95) * mm});
            skLineSegment(sketch, "E970", {"start": v(7.15, -72.95) * mm, "end": v(7.15, -56.98) * mm});
            skLineSegment(sketch, "E971", {"start": v(7.15, -56.98) * mm, "end": v(1.25, -70.07) * mm});
            skLineSegment(sketch, "E972", {"start": v(1.25, -70.07) * mm, "end": v(-0.53, -70.07) * mm});
            skLineSegment(sketch, "E973", {"start": v(-0.53, -70.07) * mm, "end": v(-6.66, -56.49) * mm});
            skLineSegment(sketch, "E974", {"start": v(-6.66, -56.49) * mm, "end": v(-6.66, -72.95) * mm});
            skLineSegment(sketch, "E975", {"start": v(-6.66, -72.95) * mm, "end": v(-8.63, -72.95) * mm});
            skLineSegment(sketch, "E976", {"start": v(-44.6, 57.48) * mm, "end": v(-44.6, 72.24) * mm});
            skLineSegment(sketch, "E977", {"start": v(-44.6, 72.24) * mm, "end": v(-42.52, 72.24) * mm});
            skLineSegment(sketch, "E978", {"start": v(-42.52, 72.24) * mm, "end": v(-42.52, 57.48) * mm});
            skArc(sketch, "E979", {"start": v(-44.6, 57.48) * mm, "mid": v(-37.32, 50.77) * mm, "end": v(-30.04, 57.48) * mm});
            skArc(sketch, "E980", {"start": v(-42.52, 57.48) * mm, "mid": v(-37.41, 52.85) * mm, "end": v(-32.3, 57.48) * mm});
            skLineSegment(sketch, "E981", {"start": v(-32.3, 57.48) * mm, "end": v(-32.3, 72.24) * mm});
            skLineSegment(sketch, "E982", {"start": v(-32.3, 72.24) * mm, "end": v(-30.04, 72.24) * mm});
            skLineSegment(sketch, "E983", {"start": v(-30.04, 72.24) * mm, "end": v(-30.04, 57.48) * mm});
            skLineSegment(sketch, "E984", {"start": v(-6.84, -190.7) * mm, "end": v(-6.84, -175.95) * mm});
            skLineSegment(sketch, "E985", {"start": v(-6.84, -175.95) * mm, "end": v(-4.76, -175.95) * mm});
            skLineSegment(sketch, "E986", {"start": v(-4.76, -175.95) * mm, "end": v(-4.76, -190.7) * mm});
            skArc(sketch, "E987", {"start": v(-6.85, -190.7) * mm, "mid": v(0.44, -197.42) * mm, "end": v(7.72, -190.7) * mm});
            skArc(sketch, "E988", {"start": v(-4.76, -190.7) * mm, "mid": v(0.34, -195.34) * mm, "end": v(5.45, -190.7) * mm});
            skLineSegment(sketch, "E989", {"start": v(5.45, -190.7) * mm, "end": v(5.45, -175.95) * mm});
            skLineSegment(sketch, "E990", {"start": v(5.45, -175.95) * mm, "end": v(7.72, -175.95) * mm});
            skLineSegment(sketch, "E991", {"start": v(7.72, -175.95) * mm, "end": v(7.72, -190.7) * mm});
            skLineSegment(sketch, "E992", {"start": v(106.17, -190.63) * mm, "end": v(106.17, -175.88) * mm});
            skLineSegment(sketch, "E993", {"start": v(106.17, -175.88) * mm, "end": v(108.25, -175.88) * mm});
            skLineSegment(sketch, "E994", {"start": v(108.25, -175.88) * mm, "end": v(108.25, -190.63) * mm});
            skArc(sketch, "E995", {"start": v(106.17, -190.63) * mm, "mid": v(113.46, -197.34) * mm, "end": v(120.74, -190.63) * mm});
            skArc(sketch, "E996", {"start": v(108.25, -190.63) * mm, "mid": v(113.36, -195.27) * mm, "end": v(118.47, -190.63) * mm});
            skLineSegment(sketch, "E997", {"start": v(118.47, -190.63) * mm, "end": v(118.47, -175.88) * mm});
            skLineSegment(sketch, "E998", {"start": v(118.47, -175.88) * mm, "end": v(120.74, -175.88) * mm});
            skLineSegment(sketch, "E999", {"start": v(120.74, -175.88) * mm, "end": v(120.74, -190.63) * mm});
            skLineSegment(sketch, "E1000", {"start": v(118.62, -99.59) * mm, "end": v(120.8, -99.59) * mm});
            skLineSegment(sketch, "E1001", {"start": v(118.77, -107.88) * mm, "end": v(120.7, -107.88) * mm});
            skLineSegment(sketch, "E1002", {"start": v(108.4, -99.36) * mm, "end": v(108.4, -106.48) * mm});
            skLineSegment(sketch, "E1003", {"start": v(106.29, -99.59) * mm, "end": v(106.29, -107.99) * mm});
            skArc(sketch, "E1004", {"start": v(118.62, -99.59) * mm, "mid": v(113.62, -94.86) * mm, "end": v(108.4, -99.36) * mm});
            skArc(sketch, "E1005", {"start": v(120.8, -99.6) * mm, "mid": v(113.54, -92.78) * mm, "end": v(106.29, -99.59) * mm});
            skArc(sketch, "E1006", {"start": v(108.4, -106.48) * mm, "mid": v(112.9, -112.22) * mm, "end": v(118.77, -107.88) * mm});
            skArc(sketch, "E1007", {"start": v(106.29, -107.99) * mm, "mid": v(113.55, -114.5) * mm, "end": v(120.7, -107.88) * mm});
            skLineSegment(sketch, "E1008", {"start": v(-107.52, -99.66) * mm, "end": v(-105.34, -99.66) * mm});
            skLineSegment(sketch, "E1009", {"start": v(-107.36, -107.95) * mm, "end": v(-105.44, -107.95) * mm});
            skLineSegment(sketch, "E1010", {"start": v(-117.73, -99.43) * mm, "end": v(-117.73, -106.55) * mm});
            skLineSegment(sketch, "E1011", {"start": v(-119.85, -99.66) * mm, "end": v(-119.85, -108.06) * mm});
            skArc(sketch, "E1012", {"start": v(-107.52, -99.66) * mm, "mid": v(-112.52, -94.93) * mm, "end": v(-117.73, -99.43) * mm});
            skArc(sketch, "E1013", {"start": v(-105.34, -99.66) * mm, "mid": v(-112.6, -92.85) * mm, "end": v(-119.85, -99.66) * mm});
            skArc(sketch, "E1014", {"start": v(-117.73, -106.55) * mm, "mid": v(-113.23, -112.29) * mm, "end": v(-107.37, -107.95) * mm});
            skArc(sketch, "E1015", {"start": v(-119.85, -108.06) * mm, "mid": v(-112.6, -114.57) * mm, "end": v(-105.44, -107.95) * mm});
            skLineSegment(sketch, "E1016", {"start": v(-118.08, 9.72) * mm, "end": v(-118.08, 30.8) * mm});
            skLineSegment(sketch, "E1017", {"start": v(-118.08, 30.8) * mm, "end": v(-115.97, 30.8) * mm});
            skLineSegment(sketch, "E1018", {"start": v(-115.97, 30.8) * mm, "end": v(-115.97, 11.65) * mm});
            skLineSegment(sketch, "E1019", {"start": v(-115.97, 11.65) * mm, "end": v(-105.07, 11.65) * mm});
            skLineSegment(sketch, "E1020", {"start": v(-105.07, 11.65) * mm, "end": v(-105.07, 9.72) * mm});
            skLineSegment(sketch, "E1021", {"start": v(-105.07, 9.72) * mm, "end": v(-118.08, 9.72) * mm});
            skLineSegment(sketch, "E1022", {"start": v(32.7, 9.75) * mm, "end": v(32.7, 30.82) * mm});
            skLineSegment(sketch, "E1023", {"start": v(32.7, 30.82) * mm, "end": v(34.82, 30.82) * mm});
            skLineSegment(sketch, "E1024", {"start": v(34.82, 30.82) * mm, "end": v(34.82, 11.68) * mm});
            skLineSegment(sketch, "E1025", {"start": v(34.82, 11.68) * mm, "end": v(45.72, 11.68) * mm});
            skLineSegment(sketch, "E1026", {"start": v(45.72, 11.68) * mm, "end": v(45.72, 9.75) * mm});
            skLineSegment(sketch, "E1027", {"start": v(45.72, 9.75) * mm, "end": v(32.7, 9.75) * mm});
            skLineSegment(sketch, "E1028", {"start": v(32.69, -114.24) * mm, "end": v(32.69, -93.17) * mm});
            skLineSegment(sketch, "E1029", {"start": v(32.69, -93.17) * mm, "end": v(34.8, -93.17) * mm});
            skLineSegment(sketch, "E1030", {"start": v(34.8, -93.17) * mm, "end": v(34.8, -112.3) * mm});
            skLineSegment(sketch, "E1031", {"start": v(34.8, -112.3) * mm, "end": v(45.7, -112.3) * mm});
            skLineSegment(sketch, "E1032", {"start": v(45.7, -112.3) * mm, "end": v(45.7, -114.24) * mm});
            skLineSegment(sketch, "E1033", {"start": v(45.7, -114.24) * mm, "end": v(32.69, -114.24) * mm});
            skLineSegment(sketch, "E1034", {"start": v(145.87, -155.78) * mm, "end": v(145.87, -134.71) * mm});
            skLineSegment(sketch, "E1035", {"start": v(145.87, -134.71) * mm, "end": v(147.99, -134.71) * mm});
            skLineSegment(sketch, "E1036", {"start": v(147.99, -134.71) * mm, "end": v(147.99, -153.85) * mm});
            skLineSegment(sketch, "E1037", {"start": v(147.99, -153.85) * mm, "end": v(158.88, -153.85) * mm});
            skLineSegment(sketch, "E1038", {"start": v(158.88, -153.85) * mm, "end": v(158.88, -155.78) * mm});
            skLineSegment(sketch, "E1039", {"start": v(158.88, -155.78) * mm, "end": v(145.87, -155.78) * mm});
            skLineSegment(sketch, "E1040", {"start": v(-183.46, -97.13) * mm, "end": v(-181.96, -95.56) * mm});
            skLineSegment(sketch, "E1041", {"start": v(-195.8, -111.66) * mm, "end": v(-194.14, -110.1) * mm});
            skArc(sketch, "E1042", {"start": v(-183.46, -97.13) * mm, "mid": v(-185.35, -95.68) * mm, "end": v(-187.67, -95.14) * mm});
            skArc(sketch, "E1043", {"start": v(-181.96, -95.56) * mm, "mid": v(-184.54, -93.64) * mm, "end": v(-187.68, -92.95) * mm});
            skLineSegment(sketch, "E1044", {"start": v(-187.67, -95.14) * mm, "end": v(-189.38, -95.14) * mm});
            skArc(sketch, "E1045", {"start": v(-189.38, -95.14) * mm, "mid": v(-192.97, -98.5) * mm, "end": v(-189.86, -102.31) * mm});
            skLineSegment(sketch, "E1046", {"start": v(-189.86, -102.31) * mm, "end": v(-186.15, -102.92) * mm});
            skLineSegment(sketch, "E1047", {"start": v(-187.68, -92.95) * mm, "end": v(-189.67, -92.95) * mm});
            skArc(sketch, "E1048", {"start": v(-189.67, -92.95) * mm, "mid": v(-195.15, -98.49) * mm, "end": v(-190.16, -104.47) * mm});
            skLineSegment(sketch, "E1049", {"start": v(-190.16, -104.47) * mm, "end": v(-186.8, -104.92) * mm});
            skArc(sketch, "E1050", {"start": v(-194.14, -110.1) * mm, "mid": v(-192.22, -111.61) * mm, "end": v(-189.9, -112.38) * mm});
            skLineSegment(sketch, "E1051", {"start": v(-189.9, -112.38) * mm, "end": v(-187.07, -112.38) * mm});
            skArc(sketch, "E1052", {"start": v(-187.07, -112.37) * mm, "mid": v(-183.38, -108.78) * mm, "end": v(-186.8, -104.92) * mm});
            skArc(sketch, "E1053", {"start": v(-195.8, -111.66) * mm, "mid": v(-193.07, -113.83) * mm, "end": v(-189.66, -114.6) * mm});
            skLineSegment(sketch, "E1054", {"start": v(-189.66, -114.6) * mm, "end": v(-187.13, -114.6) * mm});
            skArc(sketch, "E1055", {"start": v(-187.13, -114.6) * mm, "mid": v(-181.31, -109.21) * mm, "end": v(-186.15, -102.92) * mm});
            skLineSegment(sketch, "E1056", {"start": v(-32.61, -97.13) * mm, "end": v(-31.11, -95.56) * mm});
            skLineSegment(sketch, "E1057", {"start": v(-44.96, -111.65) * mm, "end": v(-43.3, -110.09) * mm});
            skArc(sketch, "E1058", {"start": v(-32.61, -97.13) * mm, "mid": v(-34.5, -95.68) * mm, "end": v(-36.82, -95.14) * mm});
            skArc(sketch, "E1059", {"start": v(-31.11, -95.56) * mm, "mid": v(-33.7, -93.64) * mm, "end": v(-36.83, -92.95) * mm});
            skLineSegment(sketch, "E1060", {"start": v(-36.82, -95.14) * mm, "end": v(-38.53, -95.14) * mm});
            skArc(sketch, "E1061", {"start": v(-38.53, -95.14) * mm, "mid": v(-42.12, -98.5) * mm, "end": v(-39, -102.3) * mm});
            skLineSegment(sketch, "E1062", {"start": v(-39, -102.3) * mm, "end": v(-35.3, -102.91) * mm});
            skLineSegment(sketch, "E1063", {"start": v(-36.83, -92.95) * mm, "end": v(-38.82, -92.95) * mm});
            skArc(sketch, "E1064", {"start": v(-38.82, -92.95) * mm, "mid": v(-44.3, -98.48) * mm, "end": v(-39.3, -104.47) * mm});
            skLineSegment(sketch, "E1065", {"start": v(-39.3, -104.47) * mm, "end": v(-35.94, -104.92) * mm});
            skArc(sketch, "E1066", {"start": v(-43.3, -110.09) * mm, "mid": v(-41.37, -111.61) * mm, "end": v(-39.04, -112.37) * mm});
            skLineSegment(sketch, "E1067", {"start": v(-39.04, -112.37) * mm, "end": v(-36.22, -112.37) * mm});
            skArc(sketch, "E1068", {"start": v(-36.22, -112.37) * mm, "mid": v(-32.53, -108.78) * mm, "end": v(-35.94, -104.92) * mm});
            skArc(sketch, "E1069", {"start": v(-44.96, -111.65) * mm, "mid": v(-42.22, -113.83) * mm, "end": v(-38.8, -114.6) * mm});
            skLineSegment(sketch, "E1070", {"start": v(-38.8, -114.6) * mm, "end": v(-36.28, -114.6) * mm});
            skArc(sketch, "E1071", {"start": v(-36.28, -114.6) * mm, "mid": v(-30.46, -109.2) * mm, "end": v(-35.3, -102.91) * mm});
            skLineSegment(sketch, "E1072", {"start": v(-183.44, -138.4) * mm, "end": v(-181.94, -136.84) * mm});
            skLineSegment(sketch, "E1073", {"start": v(-195.78, -152.93) * mm, "end": v(-194.12, -151.37) * mm});
            skArc(sketch, "E1074", {"start": v(-183.44, -138.4) * mm, "mid": v(-185.33, -136.95) * mm, "end": v(-187.65, -136.42) * mm});
            skArc(sketch, "E1075", {"start": v(-181.94, -136.84) * mm, "mid": v(-184.52, -134.91) * mm, "end": v(-187.66, -134.23) * mm});
            skLineSegment(sketch, "E1076", {"start": v(-187.65, -136.42) * mm, "end": v(-189.35, -136.42) * mm});
            skArc(sketch, "E1077", {"start": v(-189.35, -136.42) * mm, "mid": v(-192.94, -139.78) * mm, "end": v(-189.83, -143.59) * mm});
            skLineSegment(sketch, "E1078", {"start": v(-189.83, -143.59) * mm, "end": v(-186.12, -144.2) * mm});
            skLineSegment(sketch, "E1079", {"start": v(-187.66, -134.23) * mm, "end": v(-189.64, -134.23) * mm});
            skArc(sketch, "E1080", {"start": v(-189.64, -134.23) * mm, "mid": v(-195.12, -139.76) * mm, "end": v(-190.13, -145.74) * mm});
            skLineSegment(sketch, "E1081", {"start": v(-190.13, -145.74) * mm, "end": v(-186.77, -146.2) * mm});
            skArc(sketch, "E1082", {"start": v(-194.12, -151.37) * mm, "mid": v(-192.2, -152.89) * mm, "end": v(-189.87, -153.65) * mm});
            skLineSegment(sketch, "E1083", {"start": v(-189.87, -153.65) * mm, "end": v(-187.04, -153.65) * mm});
            skArc(sketch, "E1084", {"start": v(-187.04, -153.65) * mm, "mid": v(-183.35, -150.06) * mm, "end": v(-186.77, -146.2) * mm});
            skArc(sketch, "E1085", {"start": v(-195.78, -152.93) * mm, "mid": v(-193.04, -155.1) * mm, "end": v(-189.63, -155.88) * mm});
            skLineSegment(sketch, "E1086", {"start": v(-189.63, -155.88) * mm, "end": v(-187.1, -155.88) * mm});
            skArc(sketch, "E1087", {"start": v(-187.1, -155.88) * mm, "mid": v(-181.29, -150.49) * mm, "end": v(-186.12, -144.2) * mm});
            skLineSegment(sketch, "E1088", {"start": v(-145.73, 192.5) * mm, "end": v(-144.23, 194.06) * mm});
            skLineSegment(sketch, "E1089", {"start": v(-158.08, 177.97) * mm, "end": v(-156.41, 179.53) * mm});
            skArc(sketch, "E1090", {"start": v(-145.73, 192.5) * mm, "mid": v(-147.62, 193.95) * mm, "end": v(-149.94, 194.48) * mm});
            skArc(sketch, "E1091", {"start": v(-144.23, 194.06) * mm, "mid": v(-146.8, 195.98) * mm, "end": v(-149.95, 196.67) * mm});
            skLineSegment(sketch, "E1092", {"start": v(-149.94, 194.48) * mm, "end": v(-151.64, 194.48) * mm});
            skArc(sketch, "E1093", {"start": v(-151.64, 194.48) * mm, "mid": v(-155.24, 191.12) * mm, "end": v(-152.12, 187.31) * mm});
            skLineSegment(sketch, "E1094", {"start": v(-152.12, 187.31) * mm, "end": v(-148.42, 186.7) * mm});
            skLineSegment(sketch, "E1095", {"start": v(-149.95, 196.67) * mm, "end": v(-151.94, 196.67) * mm});
            skArc(sketch, "E1096", {"start": v(-151.94, 196.67) * mm, "mid": v(-157.42, 191.14) * mm, "end": v(-152.43, 185.16) * mm});
            skLineSegment(sketch, "E1097", {"start": v(-152.43, 185.16) * mm, "end": v(-149.06, 184.7) * mm});
            skArc(sketch, "E1098", {"start": v(-156.41, 179.53) * mm, "mid": v(-154.5, 178) * mm, "end": v(-152.16, 177.25) * mm});
            skLineSegment(sketch, "E1099", {"start": v(-152.16, 177.25) * mm, "end": v(-149.34, 177.25) * mm});
            skArc(sketch, "E1100", {"start": v(-149.34, 177.25) * mm, "mid": v(-145.65, 180.84) * mm, "end": v(-149.06, 184.7) * mm});
            skArc(sketch, "E1101", {"start": v(-158.08, 177.97) * mm, "mid": v(-155.34, 175.8) * mm, "end": v(-151.92, 175.02) * mm});
            skLineSegment(sketch, "E1102", {"start": v(-151.92, 175.02) * mm, "end": v(-149.4, 175.02) * mm});
            skArc(sketch, "E1103", {"start": v(-149.4, 175.02) * mm, "mid": v(-143.58, 180.41) * mm, "end": v(-148.42, 186.7) * mm});
            skLineSegment(sketch, "E1104", {"start": v(-32.64, 192.5) * mm, "end": v(-31.14, 194.07) * mm});
            skLineSegment(sketch, "E1105", {"start": v(-44.99, 177.97) * mm, "end": v(-43.32, 179.54) * mm});
            skArc(sketch, "E1106", {"start": v(-32.64, 192.5) * mm, "mid": v(-34.53, 193.95) * mm, "end": v(-36.85, 194.49) * mm});
            skArc(sketch, "E1107", {"start": v(-31.14, 194.07) * mm, "mid": v(-33.72, 196) * mm, "end": v(-36.86, 196.68) * mm});
            skLineSegment(sketch, "E1108", {"start": v(-36.85, 194.5) * mm, "end": v(-38.55, 194.5) * mm});
            skArc(sketch, "E1109", {"start": v(-38.55, 194.5) * mm, "mid": v(-42.15, 191.13) * mm, "end": v(-39.03, 187.32) * mm});
            skLineSegment(sketch, "E1110", {"start": v(-39.03, 187.32) * mm, "end": v(-35.33, 186.71) * mm});
            skLineSegment(sketch, "E1111", {"start": v(-36.86, 196.68) * mm, "end": v(-38.84, 196.68) * mm});
            skArc(sketch, "E1112", {"start": v(-38.84, 196.68) * mm, "mid": v(-44.32, 191.14) * mm, "end": v(-39.34, 185.16) * mm});
            skLineSegment(sketch, "E1113", {"start": v(-39.34, 185.16) * mm, "end": v(-35.97, 184.7) * mm});
            skArc(sketch, "E1114", {"start": v(-43.32, 179.54) * mm, "mid": v(-41.4, 178.02) * mm, "end": v(-39.07, 177.26) * mm});
            skLineSegment(sketch, "E1115", {"start": v(-39.07, 177.26) * mm, "end": v(-36.24, 177.26) * mm});
            skArc(sketch, "E1116", {"start": v(-36.25, 177.26) * mm, "mid": v(-32.56, 180.85) * mm, "end": v(-35.97, 184.7) * mm});
            skArc(sketch, "E1117", {"start": v(-44.99, 177.97) * mm, "mid": v(-42.24, 175.8) * mm, "end": v(-38.83, 175.02) * mm});
            skLineSegment(sketch, "E1118", {"start": v(-38.83, 175.02) * mm, "end": v(-36.3, 175.02) * mm});
            skArc(sketch, "E1119", {"start": v(-36.3, 175.02) * mm, "mid": v(-30.49, 180.42) * mm, "end": v(-35.33, 186.71) * mm});
            skLineSegment(sketch, "E1120", {"start": v(-105.5, -73) * mm, "end": v(-118.5, -73) * mm});
            skLineSegment(sketch, "E1121", {"start": v(-118.5, -73) * mm, "end": v(-118.5, -51.85) * mm});
            skLineSegment(sketch, "E1122", {"start": v(-118.5, -51.85) * mm, "end": v(-105.57, -51.85) * mm});
            skLineSegment(sketch, "E1123", {"start": v(-105.57, -51.85) * mm, "end": v(-105.57, -53.88) * mm});
            skLineSegment(sketch, "E1124", {"start": v(-105.57, -53.88) * mm, "end": v(-116.32, -53.88) * mm});
            skLineSegment(sketch, "E1125", {"start": v(-116.32, -53.88) * mm, "end": v(-116.32, -61.4) * mm});
            skLineSegment(sketch, "E1126", {"start": v(-116.32, -61.4) * mm, "end": v(-107.16, -61.4) * mm});
            skLineSegment(sketch, "E1127", {"start": v(-107.16, -61.4) * mm, "end": v(-107.16, -63.37) * mm});
            skLineSegment(sketch, "E1128", {"start": v(-107.16, -63.37) * mm, "end": v(-116.32, -63.37) * mm});
            skLineSegment(sketch, "E1129", {"start": v(-116.32, -63.37) * mm, "end": v(-116.32, -70.98) * mm});
            skLineSegment(sketch, "E1130", {"start": v(-116.32, -70.98) * mm, "end": v(-105.5, -70.98) * mm});
            skLineSegment(sketch, "E1131", {"start": v(-105.5, -70.98) * mm, "end": v(-105.5, -73) * mm});
            skLineSegment(sketch, "E1132", {"start": v(187.49, -114.43) * mm, "end": v(189.92, -114.43) * mm});
            skLineSegment(sketch, "E1133", {"start": v(189.92, -114.43) * mm, "end": v(189.92, -95.23) * mm});
            skLineSegment(sketch, "E1134", {"start": v(189.92, -95.23) * mm, "end": v(195.93, -95.23) * mm});
            skLineSegment(sketch, "E1135", {"start": v(195.93, -95.23) * mm, "end": v(195.93, -93.2) * mm});
            skLineSegment(sketch, "E1136", {"start": v(195.93, -93.2) * mm, "end": v(181.5, -93.2) * mm});
            skLineSegment(sketch, "E1137", {"start": v(181.5, -93.2) * mm, "end": v(181.5, -95.23) * mm});
            skLineSegment(sketch, "E1138", {"start": v(181.5, -95.23) * mm, "end": v(187.49, -95.23) * mm});
            skLineSegment(sketch, "E1139", {"start": v(187.49, -95.23) * mm, "end": v(187.49, -114.43) * mm});
            skLineSegment(sketch, "E1140", {"start": v(-81.64, 30.9) * mm, "end": v(-79.79, 30.9) * mm});
            skLineSegment(sketch, "E1141", {"start": v(-79.79, 30.9) * mm, "end": v(-79.79, 11.69) * mm});
            skLineSegment(sketch, "E1142", {"start": v(-79.79, 11.69) * mm, "end": v(-73.13, 11.69) * mm});
            skLineSegment(sketch, "E1143", {"start": v(-81.64, 30.9) * mm, "end": v(-81.64, 9.72) * mm});
            skLineSegment(sketch, "E1144", {"start": v(-81.64, 9.72) * mm, "end": v(-73.13, 9.72) * mm});
            skArc(sketch, "E1145", {"start": v(-73.13, 11.69) * mm, "mid": v(-69.61, 15.53) * mm, "end": v(-73.13, 19.37) * mm});
            skArc(sketch, "E1146", {"start": v(-73.13, 9.72) * mm, "mid": v(-67.43, 13.84) * mm, "end": v(-70.18, 20.31) * mm});
            skArc(sketch, "E1147", {"start": v(-70.18, 20.31) * mm, "mid": v(-67.84, 26.79) * mm, "end": v(-73.36, 30.9) * mm});
            skArc(sketch, "E1148", {"start": v(-73.13, 21.41) * mm, "mid": v(-69.8, 25.19) * mm, "end": v(-73.36, 28.75) * mm});
            skLineSegment(sketch, "E1149", {"start": v(-73.13, 21.4) * mm, "end": v(-77.37, 21.4) * mm});
            skLineSegment(sketch, "E1150", {"start": v(-77.37, 21.4) * mm, "end": v(-77.37, 19.37) * mm});
            skLineSegment(sketch, "E1151", {"start": v(-77.37, 19.37) * mm, "end": v(-73.13, 19.37) * mm});
            skLineSegment(sketch, "E1152", {"start": v(-73.36, 28.75) * mm, "end": v(-77.6, 28.75) * mm});
            skLineSegment(sketch, "E1153", {"start": v(-77.6, 28.75) * mm, "end": v(-77.6, 30.9) * mm});
            skLineSegment(sketch, "E1154", {"start": v(-77.6, 30.9) * mm, "end": v(-73.36, 30.9) * mm});
            skLineSegment(sketch, "E1155", {"start": v(108.32, -141.96) * mm, "end": v(108.32, -148.88) * mm});
            skLineSegment(sketch, "E1156", {"start": v(106.2, -141.96) * mm, "end": v(106.2, -148.88) * mm});
            skLineSegment(sketch, "E1157", {"start": v(118.53, -141.46) * mm, "end": v(118.53, -148.88) * mm});
            skLineSegment(sketch, "E1158", {"start": v(120.7, -141.46) * mm, "end": v(120.69, -148.88) * mm});
            skArc(sketch, "E1159", {"start": v(108.32, -148.88) * mm, "mid": v(108.49, -150.2) * mm, "end": v(109, -151.42) * mm});
            skArc(sketch, "E1160", {"start": v(106.2, -148.88) * mm, "mid": v(106.6, -151.25) * mm, "end": v(107.76, -153.36) * mm});
            skArc(sketch, "E1161", {"start": v(110.2, -152.51) * mm, "mid": v(115.54, -153.37) * mm, "end": v(118.53, -148.88) * mm});
            skArc(sketch, "E1162", {"start": v(109.07, -154.33) * mm, "mid": v(116.62, -155.3) * mm, "end": v(120.69, -148.88) * mm});
            skLineSegment(sketch, "E1163", {"start": v(107.76, -153.36) * mm, "end": v(109, -151.42) * mm});
            skLineSegment(sketch, "E1164", {"start": v(109.07, -154.33) * mm, "end": v(110.2, -152.51) * mm});
            skArc(sketch, "E1165", {"start": v(118.53, -141.46) * mm, "mid": v(118.3, -140.03) * mm, "end": v(117.62, -138.74) * mm});
            skArc(sketch, "E1166", {"start": v(120.7, -141.47) * mm, "mid": v(120.22, -139.07) * mm, "end": v(119.06, -136.93) * mm});
            skArc(sketch, "E1167", {"start": v(116.6, -137.53) * mm, "mid": v(111, -137) * mm, "end": v(108.32, -141.96) * mm});
            skArc(sketch, "E1168", {"start": v(117.93, -135.98) * mm, "mid": v(110.16, -135.23) * mm, "end": v(106.2, -141.96) * mm});
            skLineSegment(sketch, "E1169", {"start": v(116.6, -137.53) * mm, "end": v(117.93, -135.98) * mm});
            skLineSegment(sketch, "E1170", {"start": v(117.62, -138.74) * mm, "end": v(119.06, -136.93) * mm});
            skLineSegment(sketch, "E1171", {"start": v(109.42, -130.26) * mm, "end": v(109.42, -132.96) * mm});
            skLineSegment(sketch, "E1172", {"start": v(109.42, -132.96) * mm, "end": v(111.55, -132.96) * mm});
            skLineSegment(sketch, "E1173", {"start": v(111.55, -132.96) * mm, "end": v(111.55, -130.26) * mm});
            skLineSegment(sketch, "E1174", {"start": v(111.55, -130.26) * mm, "end": v(109.42, -130.26) * mm});
            skLineSegment(sketch, "E1175", {"start": v(115.38, -130.26) * mm, "end": v(115.38, -132.96) * mm});
            skLineSegment(sketch, "E1176", {"start": v(115.38, -132.96) * mm, "end": v(117.5, -132.96) * mm});
            skLineSegment(sketch, "E1177", {"start": v(117.5, -132.96) * mm, "end": v(117.5, -130.26) * mm});
            skLineSegment(sketch, "E1178", {"start": v(117.5, -130.26) * mm, "end": v(115.38, -130.26) * mm});
            skCircle(sketch, "E1179", {"center": v(-267.1, 267.2) * mm, "radius": 2.11 * mm});
            skCircle(sketch, "E1180", {"center": v(267.9, 267.16) * mm, "radius": 2.11 * mm});
            skCircle(sketch, "E1181", {"center": v(267.86, -267.88) * mm, "radius": 2.11 * mm});
            skCircle(sketch, "E1182", {"center": v(-267.14, -268) * mm, "radius": 2.11 * mm});
            skSolve(sketch);
        }
        {
            var Q0;
            Q0 = qSketchRegion(id + "F0", true);
            extrude(context, id + "F1", {"entities" : qUnion([Q0]), "depth" : 1.5 * mm});
        }
    });
